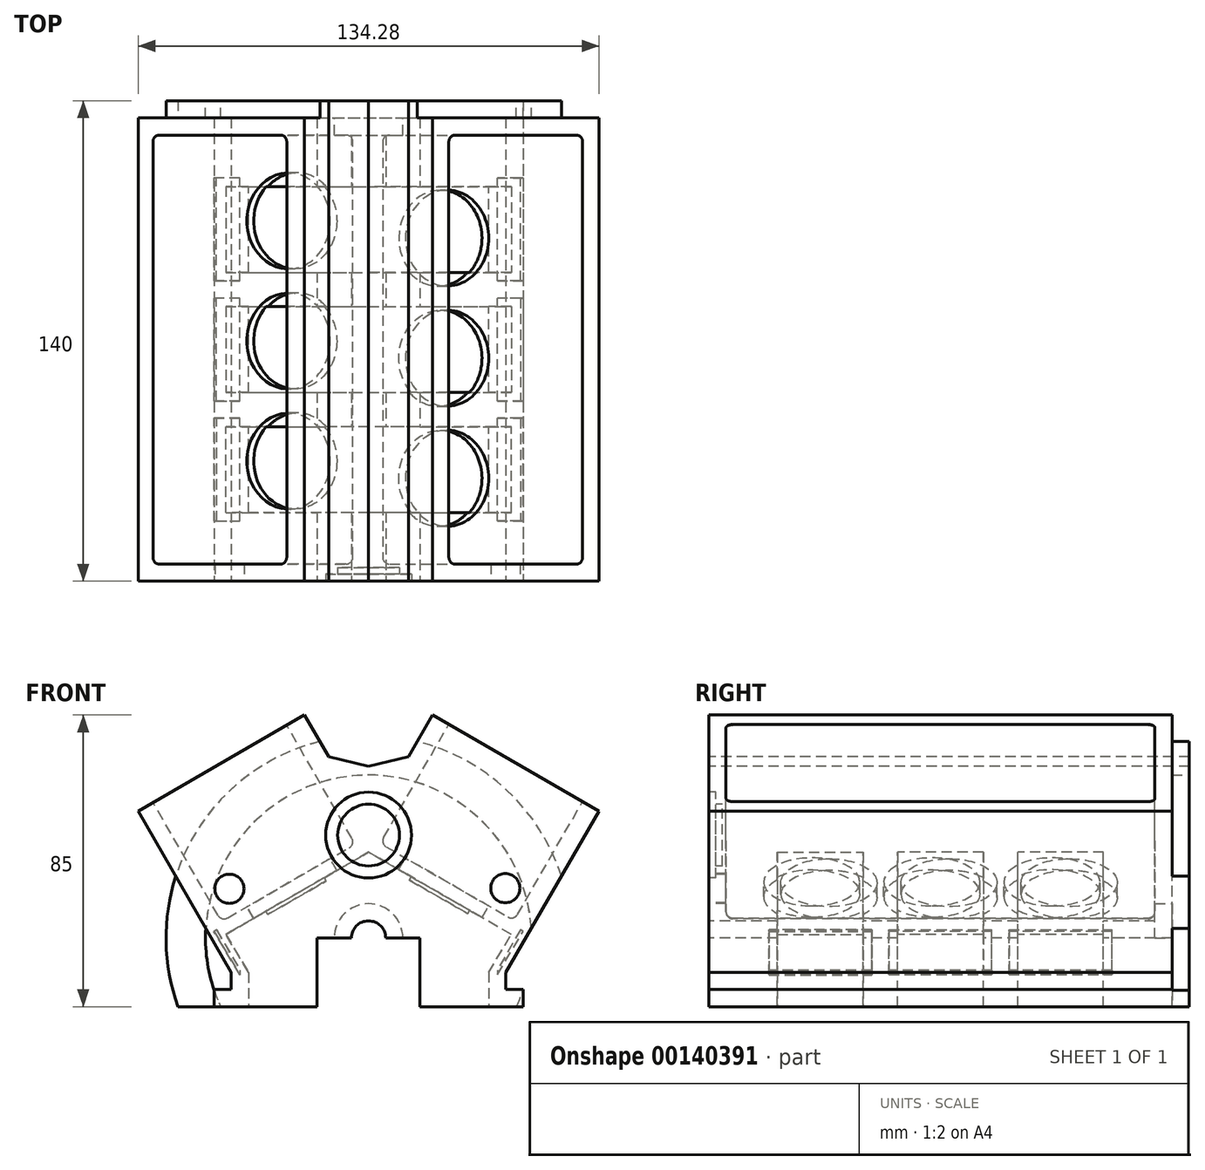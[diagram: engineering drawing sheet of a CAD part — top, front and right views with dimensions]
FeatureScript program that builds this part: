
annotation { "Feature Type Name" : "Feature", "Feature Type Description" : "" }
export const myFeature = defineFeature(function(context is Context, id is Id, definition is map)
    precondition{}
    {
        {
            var Q0;
            Q0=qCreatedBy(makeId("Front.planeOp"),FACE);
            var sketch = newSketch(context, id + "F0", { "sketchPlane" : qUnion([Q0])});
            skLineSegment(sketch, "E0", {"start": v(0, 0) * mm, "end": v(0, -20) * mm, "construction": true});
            skLineSegment(sketch, "E1", {"start": v(0, 0) * mm, "end": v(0, 50) * mm, "construction": true});
            skLineSegment(sketch, "E2", {"start": v(11.64, 52.88) * mm, "end": v(18.64, 65) * mm});
            skLineSegment(sketch, "E3", {"start": v(18.64, 65) * mm, "end": v(67.14, 37) * mm});
            skLineSegment(sketch, "E4", {"start": v(0, -20) * mm, "end": v(45, -20) * mm});
            skLineSegment(sketch, "E5", {"start": v(45, -20) * mm, "end": v(45, -15) * mm});
            skLineSegment(sketch, "E6", {"start": v(45, -15) * mm, "end": v(40, -15) * mm});
            skLineSegment(sketch, "E7", {"start": v(40, -15) * mm, "end": v(40, -10) * mm});
            skLineSegment(sketch, "E8", {"start": v(40, -10) * mm, "end": v(67.14, 37) * mm});
            skLineSegment(sketch, "E9", {"start": v(0, 50) * mm, "end": v(11.64, 52.88) * mm});
            skLineSegment(sketch, "E10.MirrorCS", {"start": v(0, 50) * mm, "end": v(-11.64, 52.88) * mm});
            skLineSegment(sketch, "E11.MirrorCS", {"start": v(-11.64, 52.88) * mm, "end": v(-18.64, 65) * mm});
            skLineSegment(sketch, "E12.MirrorCS", {"start": v(-18.64, 65) * mm, "end": v(-67.14, 37) * mm});
            skLineSegment(sketch, "E13.MirrorCS", {"start": v(-40, -10) * mm, "end": v(-67.14, 37) * mm});
            skLineSegment(sketch, "E14.MirrorCS", {"start": v(-40, -15) * mm, "end": v(-40, -10) * mm});
            skLineSegment(sketch, "E15.MirrorCS", {"start": v(-45, -15) * mm, "end": v(-40, -15) * mm});
            skLineSegment(sketch, "E16.MirrorCS", {"start": v(-45, -20) * mm, "end": v(-45, -15) * mm});
            skLineSegment(sketch, "E17.MirrorCS", {"start": v(0, -20) * mm, "end": v(-45, -20) * mm});
            skSolve(sketch);
        }
        {
            var Q0;
            Q0=makeQuery(id+"F0.imprint","IMPRINT",FACE,{"disambiguationData":[TD([[makeQuery(id+"F0.imprint","IMPRINT",EDGE,{"derivedFrom":sQuery(id+"F0.wireOp",EDGE,"E2")}),-1.0]])]});
            extrude(context, id + "F1", {"entities" : qUnion([Q0]), "oppositeDirection" : true, "depth" : 135 * mm});
        }
        {
            var Q0;
            Q0=makeQuery(id+"F1.opExtrude","SWEPT_FACE",FACE,{"disambiguationData":[OSD([sQuery(id+"F0.wireOp",EDGE,"E4"),sQuery(id+"F0.wireOp",EDGE,"E17.MirrorCS")])]});
            var sketch = newSketch(context, id + "F2", { "sketchPlane" : qUnion([Q0])});
            skLineSegment(sketch, "E18.bottom", {"start": v(-35, -20) * mm, "end": v(35, -20) * mm});
            skLineSegment(sketch, "E18.top", {"start": v(-35, -45) * mm, "end": v(35, -45) * mm});
            skLineSegment(sketch, "E18.left", {"start": v(-35, -20) * mm, "end": v(-35, -45) * mm});
            skLineSegment(sketch, "E18.right", {"start": v(35, -20) * mm, "end": v(35, -45) * mm});
            skPoint(sketch, "E18.middle", {"position": v(0, -32.5) * mm});
            skLineSegment(sketch, "E19.bottom", {"start": v(-35, -55) * mm, "end": v(35, -55) * mm});
            skLineSegment(sketch, "E19.top", {"start": v(-35, -80) * mm, "end": v(35, -80) * mm});
            skLineSegment(sketch, "E19.left", {"start": v(-35, -55) * mm, "end": v(-35, -80) * mm});
            skLineSegment(sketch, "E19.right", {"start": v(35, -55) * mm, "end": v(35, -80) * mm});
            skPoint(sketch, "E19.middle", {"position": v(0, -67.5) * mm});
            skLineSegment(sketch, "E20.bottom", {"start": v(-35, -90) * mm, "end": v(35, -90) * mm});
            skLineSegment(sketch, "E20.top", {"start": v(-35, -115) * mm, "end": v(35, -115) * mm});
            skLineSegment(sketch, "E20.left", {"start": v(-35, -90) * mm, "end": v(-35, -115) * mm});
            skLineSegment(sketch, "E20.right", {"start": v(35, -90) * mm, "end": v(35, -115) * mm});
            skPoint(sketch, "E20.middle", {"position": v(0, -102.5) * mm});
            skPoint(sketch, "E20.middle.positionSnap0", {"position": v(0, -80) * mm});
            skPoint(sketch, "E20.centerSnap0", {"position": v(0, -80) * mm});
            skSolve(sketch);
        }
        {
            var Q0;
            Q0 = qSketchRegion(id + "F2", true);
            extrude(context, id + "F3", {"entities" : qUnion([Q0]), "operationType" : NewBodyOperationType.REMOVE, "oppositeDirection" : true, "depth" : 10 * mm});
        }
        {
            var Q0;
            Q0=makeQuery(id+"F1.opExtrude","SWEPT_FACE",FACE,{"disambiguationData":[OSD([sQuery(id+"F0.wireOp",EDGE,"E3")])]});
            var sketch = newSketch(context, id + "F4", { "sketchPlane" : qUnion([Q0])});
            skLineSegment(sketch, "E21.bottom", {"start": v(-10.86, 130) * mm, "end": v(34.14, 130) * mm});
            skLineSegment(sketch, "E21.top", {"start": v(-10.86, 5) * mm, "end": v(34.14, 5) * mm});
            skLineSegment(sketch, "E21.left", {"start": v(-10.86, 130) * mm, "end": v(-10.86, 5) * mm});
            skLineSegment(sketch, "E21.right", {"start": v(34.14, 130) * mm, "end": v(34.14, 5) * mm});
            skPoint(sketch, "E21.middle.positionSnap0", {"position": v(11.64, 0) * mm});
            skPoint(sketch, "E21.centerSnap0", {"position": v(11.64, 0) * mm});
            skSolve(sketch);
        }
        {
            var Q0;
            Q0=makeQuery(id+"F4.imprint","IMPRINT",FACE,{"disambiguationData":[TD([[makeQuery(id+"F4.imprint","IMPRINT",EDGE,{"derivedFrom":sQuery(id+"F4.wireOp",EDGE,"E21.bottom")}),-1.0]])]});
            extrude(context, id + "F5", {"entities" : qUnion([Q0]), "operationType" : NewBodyOperationType.REMOVE, "oppositeDirection" : true, "depth" : 40 * mm});
        }
        {
            var Q0;
            Q0=makeQuery(id+"F1.opExtrude","SWEPT_FACE",FACE,{"disambiguationData":[OSD([sQuery(id+"F0.wireOp",EDGE,"E12.MirrorCS")])]});
            var sketch = newSketch(context, id + "F6", { "sketchPlane" : qUnion([Q0])});
            skLineSegment(sketch, "E22.bottom", {"start": v(-34.64, 130) * mm, "end": v(10.36, 130) * mm});
            skLineSegment(sketch, "E22.top", {"start": v(-34.64, 5) * mm, "end": v(10.36, 5) * mm});
            skLineSegment(sketch, "E22.left", {"start": v(-34.64, 130) * mm, "end": v(-34.64, 5) * mm});
            skLineSegment(sketch, "E22.right", {"start": v(10.36, 130) * mm, "end": v(10.36, 5) * mm});
            skPoint(sketch, "E22.middle", {"position": v(-12.14, 67.5) * mm});
            skPoint(sketch, "E22.middle.positionSnap0", {"position": v(-39.64, 67.5) * mm});
            skPoint(sketch, "E22.centerSnap0", {"position": v(-39.64, 67.5) * mm});
            skSolve(sketch);
        }
        {
            var Q0;
            Q0=makeQuery(id+"F6.imprint","IMPRINT",FACE,{"disambiguationData":[TD([[makeQuery(id+"F6.imprint","IMPRINT",EDGE,{"derivedFrom":sQuery(id+"F6.wireOp",EDGE,"E22.bottom")}),-1.0]])]});
            extrude(context, id + "F7", {"entities" : qUnion([Q0]), "operationType" : NewBodyOperationType.REMOVE, "oppositeDirection" : true, "depth" : 40 * mm});
        }
        {
            var Q0;
            Q0=makeQuery(id+"F1.opExtrude","CAP_FACE",FACE,{"disambiguationData":[OSD([sQuery(id+"F0.wireOp",EDGE,"E2"),sQuery(id+"F0.wireOp",EDGE,"E3"),sQuery(id+"F0.wireOp",EDGE,"E4"),sQuery(id+"F0.wireOp",EDGE,"E5"),sQuery(id+"F0.wireOp",EDGE,"E6"),sQuery(id+"F0.wireOp",EDGE,"E7"),sQuery(id+"F0.wireOp",EDGE,"E8"),sQuery(id+"F0.wireOp",EDGE,"E9"),sQuery(id+"F0.wireOp",EDGE,"E10.MirrorCS"),sQuery(id+"F0.wireOp",EDGE,"E11.MirrorCS"),sQuery(id+"F0.wireOp",EDGE,"E12.MirrorCS"),sQuery(id+"F0.wireOp",EDGE,"E13.MirrorCS"),sQuery(id+"F0.wireOp",EDGE,"E14.MirrorCS"),sQuery(id+"F0.wireOp",EDGE,"E15.MirrorCS"),sQuery(id+"F0.wireOp",EDGE,"E16.MirrorCS"),sQuery(id+"F0.wireOp",EDGE,"E17.MirrorCS")])],"isStart":true});
            var sketch = newSketch(context, id + "F8", { "sketchPlane" : qUnion([Q0])});
            skCircle(sketch, "E23", {"center": v(0, 0) * mm, "radius": 5 * mm});
            skSolve(sketch);
        }
        {
            var Q0;
            Q0=makeQuery(id+"F8.imprint","IMPRINT",FACE,{"disambiguationData":[TD([[makeQuery(id+"F8.imprint","IMPRINT",EDGE,{"derivedFrom":sQuery(id+"F8.wireOp",EDGE,"E23")}),1.0]])]});
            extrude(context, id + "F9", {"entities" : qUnion([Q0]), "operationType" : NewBodyOperationType.REMOVE, "oppositeDirection" : true, "depth" : 135 * mm});
        }
        {
            var Q0;
            Q0=makeQuery(id+"F1.opExtrude","CAP_FACE",FACE,{"disambiguationData":[OSD([sQuery(id+"F0.wireOp",EDGE,"E2"),sQuery(id+"F0.wireOp",EDGE,"E3"),sQuery(id+"F0.wireOp",EDGE,"E4"),sQuery(id+"F0.wireOp",EDGE,"E5"),sQuery(id+"F0.wireOp",EDGE,"E6"),sQuery(id+"F0.wireOp",EDGE,"E7"),sQuery(id+"F0.wireOp",EDGE,"E8"),sQuery(id+"F0.wireOp",EDGE,"E9"),sQuery(id+"F0.wireOp",EDGE,"E10.MirrorCS"),sQuery(id+"F0.wireOp",EDGE,"E11.MirrorCS"),sQuery(id+"F0.wireOp",EDGE,"E12.MirrorCS"),sQuery(id+"F0.wireOp",EDGE,"E13.MirrorCS"),sQuery(id+"F0.wireOp",EDGE,"E14.MirrorCS"),sQuery(id+"F0.wireOp",EDGE,"E15.MirrorCS"),sQuery(id+"F0.wireOp",EDGE,"E16.MirrorCS"),sQuery(id+"F0.wireOp",EDGE,"E17.MirrorCS")])],"isStart":true});
            var sketch = newSketch(context, id + "F10", { "sketchPlane" : qUnion([Q0])});
            skLineSegment(sketch, "E24.bottom", {"start": v(-15, 0) * mm, "end": v(15, 0) * mm});
            skLineSegment(sketch, "E24.top", {"start": v(-15, -20) * mm, "end": v(15, -20) * mm});
            skLineSegment(sketch, "E24.left", {"start": v(-15, 0) * mm, "end": v(-15, -20) * mm});
            skLineSegment(sketch, "E24.right", {"start": v(15, 0) * mm, "end": v(15, -20) * mm});
            skSolve(sketch);
        }
        {
            var Q0;
            Q0=makeQuery(id+"F10.imprint","IMPRINT",FACE,{"disambiguationData":[TD([[makeQuery(id+"F10.imprint","IMPRINT",EDGE,{"derivedFrom":sQuery(id+"F10.wireOp",EDGE,"E24.top")}),-1.0]])]});
            extrude(context, id + "F11", {"entities" : qUnion([Q0]), "operationType" : NewBodyOperationType.REMOVE, "oppositeDirection" : true, "depth" : 135 * mm});
        }
        {
            var Q0;
            Q0=makeQuery(id+"F5.boolean.opBoolean","COPY",FACE,{"derivedFrom":makeQuery(id+"F5.opExtrude","CAP_FACE",FACE,{"disambiguationData":[OSD([sQuery(id+"F4.wireOp",EDGE,"E21.bottom"),sQuery(id+"F4.wireOp",EDGE,"E21.top"),sQuery(id+"F4.wireOp",EDGE,"E21.left"),sQuery(id+"F4.wireOp",EDGE,"E21.right")])],"isStart":false})});
            var sketch = newSketch(context, id + "F12", { "sketchPlane" : qUnion([Q0])});
            skCircle(sketch, "E25", {"center": v(11.64, 30) * mm, "radius": 14 * mm});
            skCircle(sketch, "E26", {"center": v(11.64, 65) * mm, "radius": 14 * mm});
            skCircle(sketch, "E27", {"center": v(11.64, 100) * mm, "radius": 14 * mm});
            skSolve(sketch);
        }
        {
            var Q0;
            Q0=makeQuery(id+"F12.imprint","IMPRINT",FACE,{"disambiguationData":[TD([[makeQuery(id+"F12.imprint","IMPRINT",EDGE,{"derivedFrom":sQuery(id+"F12.wireOp",EDGE,"E25")}),1.0]])]});
            var Q1;
            Q1=makeQuery(id+"F12.imprint","IMPRINT",FACE,{"disambiguationData":[TD([[makeQuery(id+"F12.imprint","IMPRINT",EDGE,{"derivedFrom":sQuery(id+"F12.wireOp",EDGE,"E26")}),1.0]])]});
            var Q2;
            Q2=makeQuery(id+"F12.imprint","IMPRINT",FACE,{"disambiguationData":[TD([[makeQuery(id+"F12.imprint","IMPRINT",EDGE,{"derivedFrom":sQuery(id+"F12.wireOp",EDGE,"E27")}),1.0]])]});
            extrude(context, id + "F13", {"entities" : qUnion([Q0, Q1, Q2]), "operationType" : NewBodyOperationType.REMOVE, "oppositeDirection" : true, "depth" : 5 * mm});
        }
        {
            var Q0;
            Q0=makeQuery(id+"F7.boolean.opBoolean","COPY",FACE,{"derivedFrom":makeQuery(id+"F7.opExtrude","CAP_FACE",FACE,{"disambiguationData":[OSD([sQuery(id+"F6.wireOp",EDGE,"E22.bottom"),sQuery(id+"F6.wireOp",EDGE,"E22.top"),sQuery(id+"F6.wireOp",EDGE,"E22.left"),sQuery(id+"F6.wireOp",EDGE,"E22.right")])],"isStart":false})});
            var sketch = newSketch(context, id + "F14", { "sketchPlane" : qUnion([Q0])});
            skCircle(sketch, "E28", {"center": v(-12.14, 105) * mm, "radius": 14 * mm});
            skCircle(sketch, "E29", {"center": v(-12.14, 70) * mm, "radius": 14 * mm});
            skCircle(sketch, "E30", {"center": v(-12.14, 35) * mm, "radius": 14 * mm});
            skSolve(sketch);
        }
        {
            var Q0;
            Q0=makeQuery(id+"F14.imprint","IMPRINT",FACE,{"disambiguationData":[TD([[makeQuery(id+"F14.imprint","IMPRINT",EDGE,{"derivedFrom":sQuery(id+"F14.wireOp",EDGE,"E28")}),1.0]])]});
            var Q1;
            Q1=makeQuery(id+"F14.imprint","IMPRINT",FACE,{"disambiguationData":[TD([[makeQuery(id+"F14.imprint","IMPRINT",EDGE,{"derivedFrom":sQuery(id+"F14.wireOp",EDGE,"E29")}),1.0]])]});
            var Q2;
            Q2=makeQuery(id+"F14.imprint","IMPRINT",FACE,{"disambiguationData":[TD([[makeQuery(id+"F14.imprint","IMPRINT",EDGE,{"derivedFrom":sQuery(id+"F14.wireOp",EDGE,"E30")}),1.0]])]});
            extrude(context, id + "F15", {"entities" : qUnion([Q0, Q1, Q2]), "operationType" : NewBodyOperationType.REMOVE, "oppositeDirection" : true, "depth" : 5 * mm});
        }
        {
            var Q0;
            {var subQ0=sQuery(id+"F2.wireOp",EDGE,"E18.right");var subQ1=sQuery(id+"F2.wireOp",EDGE,"E18.top");Q0=makeQuery(id+"F11.boolean.opBoolean","SPLIT",FACE,{"disambiguationData":[TD([makeQuery(id+"F3.boolean.opBoolean","COPY",FACE,{"derivedFrom":makeQuery(id+"F3.opExtrude","SWEPT_FACE",FACE,{"disambiguationData":[OSD([subQ0])]})})])],"derivedFrom":makeQuery(id+"F3.boolean.opBoolean","COPY",FACE,{"derivedFrom":makeQuery(id+"F3.opExtrude","SWEPT_FACE",FACE,{"disambiguationData":[OSD([subQ1])]})})});}
            var sketch = newSketch(context, id + "F16", { "sketchPlane" : qUnion([Q0])});
            skLineSegment(sketch, "E31", {"start": v(35, -10) * mm, "end": v(41.62, 1.07) * mm});
            skLineSegment(sketch, "E32", {"start": v(41.62, 1.07) * mm, "end": v(0, 24.98) * mm});
            skLineSegment(sketch, "E33", {"start": v(0, 24.98) * mm, "end": v(-41.6, 1.04) * mm});
            skLineSegment(sketch, "E34", {"start": v(-41.6, 1.04) * mm, "end": v(-35, -10.05) * mm});
            skLineSegment(sketch, "E35", {"start": v(-35, -10.05) * mm, "end": v(35, -10) * mm});
            skLineSegment(sketch, "E36", {"start": v(0, 24.98) * mm, "end": v(0.02, -10.02) * mm, "construction": true});
            skSolve(sketch);
        }
        {
            var Q0;
            Q0=makeQuery(id+"F16.imprint","IMPRINT",FACE,{"disambiguationData":[TD([[makeQuery(id+"F16.imprint","IMPRINT",EDGE,{"derivedFrom":sQuery(id+"F16.wireOp",EDGE,"E31")}),1.0]])]});
            extrude(context, id + "F17", {"entities" : qUnion([Q0]), "operationType" : NewBodyOperationType.REMOVE, "depth" : 25 * mm});
        }
        {
            var Q0;
            {var subQ0=sQuery(id+"F2.wireOp",EDGE,"E19.right");var subQ1=sQuery(id+"F2.wireOp",EDGE,"E19.bottom");Q0=makeQuery(id+"F11.boolean.opBoolean","SPLIT",FACE,{"disambiguationData":[TD([makeQuery(id+"F3.boolean.opBoolean","COPY",FACE,{"derivedFrom":makeQuery(id+"F3.opExtrude","SWEPT_FACE",FACE,{"disambiguationData":[OSD([subQ0])]})})])],"derivedFrom":makeQuery(id+"F3.boolean.opBoolean","COPY",FACE,{"derivedFrom":makeQuery(id+"F3.opExtrude","SWEPT_FACE",FACE,{"disambiguationData":[OSD([subQ1])]})})});}
            var sketch = newSketch(context, id + "F18", { "sketchPlane" : qUnion([Q0])});
            skLineSegment(sketch, "E37", {"start": v(-35, -10) * mm, "end": v(35, -10) * mm});
            skLineSegment(sketch, "E38", {"start": v(35, -10) * mm, "end": v(41.61, 1.08) * mm});
            skLineSegment(sketch, "E39", {"start": v(41.61, 1.08) * mm, "end": v(0, 25) * mm});
            skLineSegment(sketch, "E40", {"start": v(0, 25) * mm, "end": v(-41.61, 1.08) * mm});
            skLineSegment(sketch, "E41", {"start": v(-41.61, 1.08) * mm, "end": v(-35, -10) * mm});
            skLineSegment(sketch, "E42", {"start": v(0, 25) * mm, "end": v(0, -10) * mm, "construction": true});
            skSolve(sketch);
        }
        {
            var Q0;
            Q0 = qSketchRegion(id + "F18", true);
            extrude(context, id + "F19", {"entities" : qUnion([Q0]), "operationType" : NewBodyOperationType.REMOVE, "depth" : 25 * mm});
        }
        {
            var Q0;
            {var subQ0=sQuery(id+"F2.wireOp",EDGE,"E20.right");var subQ1=sQuery(id+"F2.wireOp",EDGE,"E20.bottom");Q0=makeQuery(id+"F11.boolean.opBoolean","SPLIT",FACE,{"disambiguationData":[TD([makeQuery(id+"F3.boolean.opBoolean","COPY",FACE,{"derivedFrom":makeQuery(id+"F3.opExtrude","SWEPT_FACE",FACE,{"disambiguationData":[OSD([subQ0])]})})])],"derivedFrom":makeQuery(id+"F3.boolean.opBoolean","COPY",FACE,{"derivedFrom":makeQuery(id+"F3.opExtrude","SWEPT_FACE",FACE,{"disambiguationData":[OSD([subQ1])]})})});}
            var sketch = newSketch(context, id + "F20", { "sketchPlane" : qUnion([Q0])});
            skLineSegment(sketch, "E43", {"start": v(-35, -10) * mm, "end": v(35, -10) * mm});
            skLineSegment(sketch, "E44", {"start": v(0, 25) * mm, "end": v(0, -10) * mm, "construction": true});
            skLineSegment(sketch, "E45", {"start": v(-35, -10) * mm, "end": v(-41.61, 1.08) * mm});
            skLineSegment(sketch, "E46", {"start": v(-41.61, 1.08) * mm, "end": v(0, 25) * mm});
            skLineSegment(sketch, "E47", {"start": v(35, -10) * mm, "end": v(41.61, 1.08) * mm});
            skLineSegment(sketch, "E48", {"start": v(41.61, 1.08) * mm, "end": v(0, 25) * mm});
            skSolve(sketch);
        }
        {
            var Q0;
            {var subQ0=sQuery(id+"F20.wireOp",EDGE,"E45");Q0=makeQuery(id+"F20.imprint","IMPRINT",FACE,{"disambiguationData":[TD([[makeQuery(id+"F20.imprint","IMPRINT",EDGE,{"derivedFrom":subQ0}),-1.0]])]});}
            extrude(context, id + "F21", {"entities" : qUnion([Q0]), "operationType" : NewBodyOperationType.REMOVE, "depth" : 25 * mm});
        }
        {
            var Q0;
            Q0=makeQuery(id+"F5.boolean.opBoolean","COPY",EDGE,{"derivedFrom":makeQuery(id+"F5.opExtrude","SWEPT_EDGE",EDGE,{"disambiguationData":[OSD([sQuery(id+"F4.wireOp",EDGE,"E21.bottom"),sQuery(id+"F4.wireOp",EDGE,"E21.left")])]})});
            var Q1;
            Q1=makeQuery(id+"F5.boolean.opBoolean","COPY",EDGE,{"derivedFrom":makeQuery(id+"F5.opExtrude","CAP_EDGE",EDGE,{"disambiguationData":[OSD([sQuery(id+"F4.wireOp",EDGE,"E21.bottom")])],"isStart":false})});
            var Q2;
            Q2=makeQuery(id+"F5.boolean.opBoolean","COPY",EDGE,{"derivedFrom":makeQuery(id+"F5.opExtrude","CAP_EDGE",EDGE,{"disambiguationData":[OSD([sQuery(id+"F4.wireOp",EDGE,"E21.left")])],"isStart":false})});
            var Q3;
            Q3=makeQuery(id+"F5.boolean.opBoolean","COPY",EDGE,{"derivedFrom":makeQuery(id+"F5.opExtrude","CAP_EDGE",EDGE,{"disambiguationData":[OSD([sQuery(id+"F4.wireOp",EDGE,"E21.top")])],"isStart":false})});
            var Q4;
            Q4=makeQuery(id+"F5.boolean.opBoolean","COPY",EDGE,{"derivedFrom":makeQuery(id+"F5.opExtrude","SWEPT_EDGE",EDGE,{"disambiguationData":[OSD([sQuery(id+"F4.wireOp",EDGE,"E21.top"),sQuery(id+"F4.wireOp",EDGE,"E21.left")])]})});
            var Q5;
            Q5=makeQuery(id+"F5.boolean.opBoolean","COPY",EDGE,{"derivedFrom":makeQuery(id+"F5.opExtrude","SWEPT_EDGE",EDGE,{"disambiguationData":[OSD([sQuery(id+"F4.wireOp",EDGE,"E21.bottom"),sQuery(id+"F4.wireOp",EDGE,"E21.right")])]})});
            var Q6;
            Q6=makeQuery(id+"F5.boolean.opBoolean","COPY",EDGE,{"derivedFrom":makeQuery(id+"F5.opExtrude","CAP_EDGE",EDGE,{"disambiguationData":[OSD([sQuery(id+"F4.wireOp",EDGE,"E21.right")])],"isStart":false})});
            var Q7;
            Q7=makeQuery(id+"F5.boolean.opBoolean","COPY",EDGE,{"derivedFrom":makeQuery(id+"F5.opExtrude","SWEPT_EDGE",EDGE,{"disambiguationData":[OSD([sQuery(id+"F4.wireOp",EDGE,"E21.top"),sQuery(id+"F4.wireOp",EDGE,"E21.right")])]})});
            fillet(context, id + "F22", {"entities" : qUnion([Q0, Q1, Q2, Q3, Q4, Q5, Q6, Q7]), "radius" : 2 * mm, "tangentPropagation" : true, "allowEdgeOverflow" : false});
        }
        {
            var Q0;
            Q0=makeQuery(id+"F7.boolean.opBoolean","COPY",EDGE,{"derivedFrom":makeQuery(id+"F7.opExtrude","SWEPT_EDGE",EDGE,{"disambiguationData":[OSD([sQuery(id+"F6.wireOp",EDGE,"E22.bottom"),sQuery(id+"F6.wireOp",EDGE,"E22.left")])]})});
            var Q1;
            Q1=makeQuery(id+"F7.boolean.opBoolean","COPY",EDGE,{"derivedFrom":makeQuery(id+"F7.opExtrude","CAP_EDGE",EDGE,{"disambiguationData":[OSD([sQuery(id+"F6.wireOp",EDGE,"E22.bottom")])],"isStart":false})});
            var Q2;
            Q2=makeQuery(id+"F7.boolean.opBoolean","COPY",EDGE,{"derivedFrom":makeQuery(id+"F7.opExtrude","CAP_EDGE",EDGE,{"disambiguationData":[OSD([sQuery(id+"F6.wireOp",EDGE,"E22.left")])],"isStart":false})});
            var Q3;
            Q3=makeQuery(id+"F7.boolean.opBoolean","COPY",EDGE,{"derivedFrom":makeQuery(id+"F7.opExtrude","SWEPT_EDGE",EDGE,{"disambiguationData":[OSD([sQuery(id+"F6.wireOp",EDGE,"E22.bottom"),sQuery(id+"F6.wireOp",EDGE,"E22.right")])]})});
            var Q4;
            Q4=makeQuery(id+"F7.boolean.opBoolean","COPY",EDGE,{"derivedFrom":makeQuery(id+"F7.opExtrude","CAP_EDGE",EDGE,{"disambiguationData":[OSD([sQuery(id+"F6.wireOp",EDGE,"E22.right")])],"isStart":false})});
            var Q5;
            Q5=makeQuery(id+"F7.boolean.opBoolean","COPY",EDGE,{"derivedFrom":makeQuery(id+"F7.opExtrude","CAP_EDGE",EDGE,{"disambiguationData":[OSD([sQuery(id+"F6.wireOp",EDGE,"E22.top")])],"isStart":false})});
            var Q6;
            Q6=makeQuery(id+"F7.boolean.opBoolean","COPY",EDGE,{"derivedFrom":makeQuery(id+"F7.opExtrude","SWEPT_EDGE",EDGE,{"disambiguationData":[OSD([sQuery(id+"F6.wireOp",EDGE,"E22.top"),sQuery(id+"F6.wireOp",EDGE,"E22.left")])]})});
            var Q7;
            Q7=makeQuery(id+"F7.boolean.opBoolean","COPY",EDGE,{"derivedFrom":makeQuery(id+"F7.opExtrude","SWEPT_EDGE",EDGE,{"disambiguationData":[OSD([sQuery(id+"F6.wireOp",EDGE,"E22.top"),sQuery(id+"F6.wireOp",EDGE,"E22.right")])]})});
            fillet(context, id + "F23", {"entities" : qUnion([Q0, Q1, Q2, Q3, Q4, Q5, Q6, Q7]), "radius" : 2 * mm, "tangentPropagation" : true, "allowEdgeOverflow" : false});
        }
        {
            var Q0;
            Q0=makeQuery(id+"F5.boolean.opBoolean","COPY",FACE,{"derivedFrom":makeQuery(id+"F5.opExtrude","SWEPT_FACE",FACE,{"disambiguationData":[OSD([sQuery(id+"F4.wireOp",EDGE,"E21.top")])]})});
            var Q1;
            {var subQ2=sQuery(id+"F10.wireOp",EDGE,"E24.left");Q1=makeQuery(id+"F17.boolean.opBoolean","SPLIT",FACE,{"disambiguationData":[TD([makeQuery(id+"F3.boolean.opBoolean","COPY",FACE,{"derivedFrom":makeQuery(id+"F3.opExtrude","SWEPT_FACE",FACE,{"disambiguationData":[OSD([sQuery(id+"F2.wireOp",EDGE,"E18.bottom")])]})})])],"derivedFrom":makeQuery(id+"F11.boolean.opBoolean","COPY",FACE,{"derivedFrom":makeQuery(id+"F11.opExtrude","SWEPT_FACE",FACE,{"disambiguationData":[OSD([subQ2])]})})});}
            var Q2;
            Q2=makeQuery(id+"F1.opExtrude","SWEPT_FACE",FACE,{"disambiguationData":[OSD([sQuery(id+"F0.wireOp",EDGE,"E12.MirrorCS")])]});
            var Q3;
            Q3=makeQuery(id+"F5.boolean.opBoolean","COPY",FACE,{"derivedFrom":makeQuery(id+"F5.opExtrude","SWEPT_FACE",FACE,{"disambiguationData":[OSD([sQuery(id+"F4.wireOp",EDGE,"E21.bottom")])]})});
            var Q4;
            {var subQ0=sQuery(id+"F6.wireOp",EDGE,"E22.left");var subQ1=sQuery(id+"F6.wireOp",EDGE,"E22.bottom");Q4=makeQuery(id+"F23.opFillet","BLEND_FACE",FACE,{"disambiguationData":[OSD([subQ1,subQ0]),TDD([makeQuery(id+"F7.boolean.opBoolean","COPY",EDGE,{"derivedFrom":makeQuery(id+"F7.opExtrude","SWEPT_EDGE",EDGE,{"disambiguationData":[OSD([subQ1,subQ0])]})})])]});}
            var Q5;
            {var subQ1=sQuery(id+"F2.wireOp",EDGE,"E20.right");var subQ2=sQuery(id+"F2.wireOp",EDGE,"E20.left");var subQ3=sQuery(id+"F2.wireOp",EDGE,"E20.top");var subQ5=makeQuery(id+"F3.boolean.opBoolean","COPY",FACE,{"derivedFrom":makeQuery(id+"F3.opExtrude","SWEPT_FACE",FACE,{"disambiguationData":[OSD([subQ3])]})});Q5=makeQuery(id+"F21.boolean.opBoolean","MERGE",FACE,{"derivedFrom":[makeQuery(id+"F11.boolean.opBoolean","SPLIT",FACE,{"disambiguationData":[TD([makeQuery(id+"F3.boolean.opBoolean","COPY",FACE,{"derivedFrom":makeQuery(id+"F3.opExtrude","SWEPT_FACE",FACE,{"disambiguationData":[OSD([subQ2])]})})])],"derivedFrom":subQ5}),makeQuery(id+"F11.boolean.opBoolean","SPLIT",FACE,{"disambiguationData":[TD([makeQuery(id+"F3.boolean.opBoolean","COPY",FACE,{"derivedFrom":makeQuery(id+"F3.opExtrude","SWEPT_FACE",FACE,{"disambiguationData":[OSD([subQ1])]})})])],"derivedFrom":subQ5}),makeQuery(id+"F21.opExtrude","CAP_FACE",FACE,{"disambiguationData":[OSD([sQuery(id+"F20.wireOp",EDGE,"E43"),sQuery(id+"F20.wireOp",EDGE,"E45"),sQuery(id+"F20.wireOp",EDGE,"E46"),sQuery(id+"F20.wireOp",EDGE,"E47"),sQuery(id+"F20.wireOp",EDGE,"E48")])],"isStart":false})]});}
            var Q6;
            {var subQ1=sQuery(id+"F2.wireOp",EDGE,"E19.right");var subQ2=sQuery(id+"F2.wireOp",EDGE,"E19.left");var subQ3=sQuery(id+"F2.wireOp",EDGE,"E19.top");var subQ5=makeQuery(id+"F3.boolean.opBoolean","COPY",FACE,{"derivedFrom":makeQuery(id+"F3.opExtrude","SWEPT_FACE",FACE,{"disambiguationData":[OSD([subQ3])]})});Q6=makeQuery(id+"F19.boolean.opBoolean","MERGE",FACE,{"derivedFrom":[makeQuery(id+"F11.boolean.opBoolean","SPLIT",FACE,{"disambiguationData":[TD([makeQuery(id+"F3.boolean.opBoolean","COPY",FACE,{"derivedFrom":makeQuery(id+"F3.opExtrude","SWEPT_FACE",FACE,{"disambiguationData":[OSD([subQ2])]})})])],"derivedFrom":subQ5}),makeQuery(id+"F11.boolean.opBoolean","SPLIT",FACE,{"disambiguationData":[TD([makeQuery(id+"F3.boolean.opBoolean","COPY",FACE,{"derivedFrom":makeQuery(id+"F3.opExtrude","SWEPT_FACE",FACE,{"disambiguationData":[OSD([subQ1])]})})])],"derivedFrom":subQ5}),makeQuery(id+"F19.opExtrude","CAP_FACE",FACE,{"disambiguationData":[OSD([sQuery(id+"F18.wireOp",EDGE,"E37"),sQuery(id+"F18.wireOp",EDGE,"E38"),sQuery(id+"F18.wireOp",EDGE,"E39"),sQuery(id+"F18.wireOp",EDGE,"E40"),sQuery(id+"F18.wireOp",EDGE,"E41")])],"isStart":false})]});}
            var Q7;
            Q7=makeQuery(id+"F1.opExtrude","SWEPT_FACE",FACE,{"disambiguationData":[OSD([sQuery(id+"F0.wireOp",EDGE,"E5")])]});
            var Q8;
            {var subQ0=sQuery(id+"F0.wireOp",EDGE,"E17.MirrorCS");var subQ1=sQuery(id+"F0.wireOp",EDGE,"E16.MirrorCS");var subQ13=sQuery(id+"F0.wireOp",EDGE,"E4");Q8=makeQuery(id+"F11.boolean.opBoolean","SPLIT",FACE,{"disambiguationData":[TD([makeQuery(id+"F1.opExtrude","SWEPT_FACE",FACE,{"disambiguationData":[OSD([subQ1])]})])],"derivedFrom":makeQuery(id+"F1.opExtrude","SWEPT_FACE",FACE,{"disambiguationData":[OSD([subQ13,subQ0])]})});}
            var Q9;
            Q9=makeQuery(id+"F1.opExtrude","SWEPT_FACE",FACE,{"disambiguationData":[OSD([sQuery(id+"F0.wireOp",EDGE,"E13.MirrorCS")])]});
            var Q10;
            Q10=makeQuery(id+"F19.boolean.opBoolean","COPY",FACE,{"derivedFrom":makeQuery(id+"F19.opExtrude","SWEPT_FACE",FACE,{"disambiguationData":[OSD([sQuery(id+"F18.wireOp",EDGE,"E40")])]})});
            var Q11;
            Q11=makeQuery(id+"F1.opExtrude","SWEPT_FACE",FACE,{"disambiguationData":[OSD([sQuery(id+"F0.wireOp",EDGE,"E9")])]});
            var Q12;
            Q12=makeQuery(id+"F1.opExtrude","SWEPT_FACE",FACE,{"disambiguationData":[OSD([sQuery(id+"F0.wireOp",EDGE,"E3")])]});
            var Q13;
            Q13=makeQuery(id+"F22.opFillet","BLEND_FACE",FACE,{"disambiguationData":[OSD([sQuery(id+"F4.wireOp",EDGE,"E21.bottom")])]});
            var Q14;
            {var subQ0=sQuery(id+"F0.wireOp",EDGE,"E17.MirrorCS");var subQ12=sQuery(id+"F0.wireOp",EDGE,"E5");var subQ13=sQuery(id+"F0.wireOp",EDGE,"E4");Q14=makeQuery(id+"F11.boolean.opBoolean","SPLIT",FACE,{"disambiguationData":[TD([makeQuery(id+"F1.opExtrude","SWEPT_FACE",FACE,{"disambiguationData":[OSD([subQ12])]})])],"derivedFrom":makeQuery(id+"F1.opExtrude","SWEPT_FACE",FACE,{"disambiguationData":[OSD([subQ13,subQ0])]})});}
            var Q15;
            Q15=makeQuery(id+"F1.opExtrude","SWEPT_FACE",FACE,{"disambiguationData":[OSD([sQuery(id+"F0.wireOp",EDGE,"E10.MirrorCS")])]});
            var Q16;
            Q16=makeQuery(id+"F1.opExtrude","CAP_FACE",FACE,{"disambiguationData":[OSD([sQuery(id+"F0.wireOp",EDGE,"E2"),sQuery(id+"F0.wireOp",EDGE,"E3"),sQuery(id+"F0.wireOp",EDGE,"E4"),sQuery(id+"F0.wireOp",EDGE,"E5"),sQuery(id+"F0.wireOp",EDGE,"E6"),sQuery(id+"F0.wireOp",EDGE,"E7"),sQuery(id+"F0.wireOp",EDGE,"E8"),sQuery(id+"F0.wireOp",EDGE,"E9"),sQuery(id+"F0.wireOp",EDGE,"E10.MirrorCS"),sQuery(id+"F0.wireOp",EDGE,"E11.MirrorCS"),sQuery(id+"F0.wireOp",EDGE,"E12.MirrorCS"),sQuery(id+"F0.wireOp",EDGE,"E13.MirrorCS"),sQuery(id+"F0.wireOp",EDGE,"E14.MirrorCS"),sQuery(id+"F0.wireOp",EDGE,"E15.MirrorCS"),sQuery(id+"F0.wireOp",EDGE,"E16.MirrorCS"),sQuery(id+"F0.wireOp",EDGE,"E17.MirrorCS")])],"isStart":true});
            var Q17;
            {var subQ2=sQuery(id+"F8.wireOp",EDGE,"E23");var subQ6=makeQuery(id+"F3.boolean.opBoolean","COPY",FACE,{"derivedFrom":makeQuery(id+"F3.opExtrude","SWEPT_FACE",FACE,{"disambiguationData":[OSD([sQuery(id+"F2.wireOp",EDGE,"E19.top")])]})});var subQ9=sQuery(id+"F2.wireOp",EDGE,"E18.top");Q17=makeQuery(id+"F21.boolean.opBoolean","SPLIT",FACE,{"disambiguationData":[TD([subQ6])],"derivedFrom":makeQuery(id+"F19.boolean.opBoolean","SPLIT",FACE,{"disambiguationData":[TD([subQ6])],"derivedFrom":makeQuery(id+"F17.boolean.opBoolean","SPLIT",FACE,{"disambiguationData":[TD([makeQuery(id+"F3.boolean.opBoolean","COPY",FACE,{"derivedFrom":makeQuery(id+"F3.opExtrude","SWEPT_FACE",FACE,{"disambiguationData":[OSD([subQ9])]})})])],"derivedFrom":makeQuery(id+"F9.boolean.opBoolean","COPY",FACE,{"derivedFrom":makeQuery(id+"F9.opExtrude","SWEPT_FACE",FACE,{"disambiguationData":[OSD([subQ2])]})})})})});}
            var Q18;
            Q18=makeQuery(id+"F22.opFillet","BLEND_FACE",FACE,{"disambiguationData":[OSD([sQuery(id+"F4.wireOp",EDGE,"E21.left")])]});
            var Q19;
            Q19=makeQuery(id+"F1.opExtrude","SWEPT_FACE",FACE,{"disambiguationData":[OSD([sQuery(id+"F0.wireOp",EDGE,"E6")])]});
            var Q20;
            {var subQ0=sQuery(id+"F10.wireOp",EDGE,"E24.right");var subQ6=sQuery(id+"F2.wireOp",EDGE,"E20.top");var subQ7=makeQuery(id+"F3.boolean.opBoolean","COPY",FACE,{"derivedFrom":makeQuery(id+"F3.opExtrude","SWEPT_FACE",FACE,{"disambiguationData":[OSD([subQ6])]})});var subQ9=sQuery(id+"F2.wireOp",EDGE,"E19.top");var subQ10=makeQuery(id+"F3.boolean.opBoolean","COPY",FACE,{"derivedFrom":makeQuery(id+"F3.opExtrude","SWEPT_FACE",FACE,{"disambiguationData":[OSD([subQ9])]})});var subQ15=sQuery(id+"F2.wireOp",EDGE,"E18.top");Q20=makeQuery(id+"F21.boolean.opBoolean","SPLIT",FACE,{"disambiguationData":[TD([subQ7])],"derivedFrom":makeQuery(id+"F19.boolean.opBoolean","SPLIT",FACE,{"disambiguationData":[TD([subQ10])],"derivedFrom":makeQuery(id+"F17.boolean.opBoolean","SPLIT",FACE,{"disambiguationData":[TD([makeQuery(id+"F3.boolean.opBoolean","COPY",FACE,{"derivedFrom":makeQuery(id+"F3.opExtrude","SWEPT_FACE",FACE,{"disambiguationData":[OSD([subQ15])]})})])],"derivedFrom":makeQuery(id+"F11.boolean.opBoolean","COPY",FACE,{"derivedFrom":makeQuery(id+"F11.opExtrude","SWEPT_FACE",FACE,{"disambiguationData":[OSD([subQ0])]})})})})});}
            var Q21;
            Q21=makeQuery(id+"F1.opExtrude","SWEPT_FACE",FACE,{"disambiguationData":[OSD([sQuery(id+"F0.wireOp",EDGE,"E11.MirrorCS")])]});
            var Q22;
            Q22=makeQuery(id+"F1.opExtrude","CAP_FACE",FACE,{"disambiguationData":[OSD([sQuery(id+"F0.wireOp",EDGE,"E2"),sQuery(id+"F0.wireOp",EDGE,"E3"),sQuery(id+"F0.wireOp",EDGE,"E4"),sQuery(id+"F0.wireOp",EDGE,"E5"),sQuery(id+"F0.wireOp",EDGE,"E6"),sQuery(id+"F0.wireOp",EDGE,"E7"),sQuery(id+"F0.wireOp",EDGE,"E8"),sQuery(id+"F0.wireOp",EDGE,"E9"),sQuery(id+"F0.wireOp",EDGE,"E10.MirrorCS"),sQuery(id+"F0.wireOp",EDGE,"E11.MirrorCS"),sQuery(id+"F0.wireOp",EDGE,"E12.MirrorCS"),sQuery(id+"F0.wireOp",EDGE,"E13.MirrorCS"),sQuery(id+"F0.wireOp",EDGE,"E14.MirrorCS"),sQuery(id+"F0.wireOp",EDGE,"E15.MirrorCS"),sQuery(id+"F0.wireOp",EDGE,"E16.MirrorCS"),sQuery(id+"F0.wireOp",EDGE,"E17.MirrorCS")])],"isStart":false});
            var Q23;
            Q23=makeQuery(id+"F13.boolean.opBoolean","COPY",FACE,{"derivedFrom":makeQuery(id+"F13.opExtrude","SWEPT_FACE",FACE,{"disambiguationData":[OSD([sQuery(id+"F12.wireOp",EDGE,"E26")])]})});
            var Q24;
            Q24=makeQuery(id+"F21.boolean.opBoolean","COPY",FACE,{"derivedFrom":makeQuery(id+"F21.opExtrude","SWEPT_FACE",FACE,{"disambiguationData":[OSD([sQuery(id+"F20.wireOp",EDGE,"E46")])]})});
            var Q25;
            Q25=makeQuery(id+"F13.boolean.opBoolean","COPY",FACE,{"derivedFrom":makeQuery(id+"F13.opExtrude","SWEPT_FACE",FACE,{"disambiguationData":[OSD([sQuery(id+"F12.wireOp",EDGE,"E27")])]})});
            var Q26;
            Q26=makeQuery(id+"F1.opExtrude","SWEPT_FACE",FACE,{"disambiguationData":[OSD([sQuery(id+"F0.wireOp",EDGE,"E8")])]});
            var Q27;
            Q27=makeQuery(id+"F5.boolean.opBoolean","COPY",FACE,{"derivedFrom":makeQuery(id+"F5.opExtrude","CAP_FACE",FACE,{"disambiguationData":[OSD([sQuery(id+"F4.wireOp",EDGE,"E21.bottom"),sQuery(id+"F4.wireOp",EDGE,"E21.top"),sQuery(id+"F4.wireOp",EDGE,"E21.left"),sQuery(id+"F4.wireOp",EDGE,"E21.right")])],"isStart":false})});
            var Q28;
            {var subQ2=sQuery(id+"F8.wireOp",EDGE,"E23");var subQ7=sQuery(id+"F2.wireOp",EDGE,"E18.top");Q28=makeQuery(id+"F21.boolean.opBoolean","SPLIT",FACE,{"disambiguationData":[TD([makeQuery(id+"F3.boolean.opBoolean","COPY",FACE,{"derivedFrom":makeQuery(id+"F3.opExtrude","SWEPT_FACE",FACE,{"disambiguationData":[OSD([sQuery(id+"F2.wireOp",EDGE,"E20.top")])]})})])],"derivedFrom":makeQuery(id+"F19.boolean.opBoolean","SPLIT",FACE,{"disambiguationData":[TD([makeQuery(id+"F3.boolean.opBoolean","COPY",FACE,{"derivedFrom":makeQuery(id+"F3.opExtrude","SWEPT_FACE",FACE,{"disambiguationData":[OSD([sQuery(id+"F2.wireOp",EDGE,"E19.top")])]})})])],"derivedFrom":makeQuery(id+"F17.boolean.opBoolean","SPLIT",FACE,{"disambiguationData":[TD([makeQuery(id+"F3.boolean.opBoolean","COPY",FACE,{"derivedFrom":makeQuery(id+"F3.opExtrude","SWEPT_FACE",FACE,{"disambiguationData":[OSD([subQ7])]})})])],"derivedFrom":makeQuery(id+"F9.boolean.opBoolean","COPY",FACE,{"derivedFrom":makeQuery(id+"F9.opExtrude","SWEPT_FACE",FACE,{"disambiguationData":[OSD([subQ2])]})})})})});}
            var Q29;
            Q29=makeQuery(id+"F7.boolean.opBoolean","COPY",FACE,{"derivedFrom":makeQuery(id+"F7.opExtrude","SWEPT_FACE",FACE,{"disambiguationData":[OSD([sQuery(id+"F6.wireOp",EDGE,"E22.top")])]})});
            var Q30;
            Q30=makeQuery(id+"F7.boolean.opBoolean","COPY",FACE,{"derivedFrom":makeQuery(id+"F7.opExtrude","SWEPT_FACE",FACE,{"disambiguationData":[OSD([sQuery(id+"F6.wireOp",EDGE,"E22.bottom")])]})});
            var Q31;
            Q31=makeQuery(id+"F5.boolean.opBoolean","COPY",FACE,{"derivedFrom":makeQuery(id+"F5.opExtrude","SWEPT_FACE",FACE,{"disambiguationData":[OSD([sQuery(id+"F4.wireOp",EDGE,"E21.left")])]})});
            var Q32;
            Q32=makeQuery(id+"F5.boolean.opBoolean","COPY",FACE,{"derivedFrom":makeQuery(id+"F5.opExtrude","SWEPT_FACE",FACE,{"disambiguationData":[OSD([sQuery(id+"F4.wireOp",EDGE,"E21.right")])]})});
            var Q33;
            Q33=makeQuery(id+"F1.opExtrude","SWEPT_FACE",FACE,{"disambiguationData":[OSD([sQuery(id+"F0.wireOp",EDGE,"E7")])]});
            var Q34;
            Q34=makeQuery(id+"F7.boolean.opBoolean","COPY",FACE,{"derivedFrom":makeQuery(id+"F7.opExtrude","SWEPT_FACE",FACE,{"disambiguationData":[OSD([sQuery(id+"F6.wireOp",EDGE,"E22.left")])]})});
            var Q35;
            Q35=makeQuery(id+"F7.boolean.opBoolean","COPY",FACE,{"derivedFrom":makeQuery(id+"F7.opExtrude","SWEPT_FACE",FACE,{"disambiguationData":[OSD([sQuery(id+"F6.wireOp",EDGE,"E22.right")])]})});
            var Q36;
            {var subQ0=sQuery(id+"F4.wireOp",EDGE,"E21.left");var subQ1=sQuery(id+"F4.wireOp",EDGE,"E21.bottom");Q36=makeQuery(id+"F22.opFillet","BLEND_FACE",FACE,{"disambiguationData":[OSD([subQ1,subQ0]),TDD([makeQuery(id+"F5.boolean.opBoolean","COPY",EDGE,{"derivedFrom":makeQuery(id+"F5.opExtrude","SWEPT_EDGE",EDGE,{"disambiguationData":[OSD([subQ1,subQ0])]})})])]});}
            var Q37;
            {var subQ0=sQuery(id+"F4.wireOp",EDGE,"E21.right");var subQ1=sQuery(id+"F4.wireOp",EDGE,"E21.bottom");Q37=makeQuery(id+"F22.opFillet","BLEND_FACE",FACE,{"disambiguationData":[OSD([subQ1,subQ0]),TDD([makeQuery(id+"F5.boolean.opBoolean","COPY",EDGE,{"derivedFrom":makeQuery(id+"F5.opExtrude","SWEPT_EDGE",EDGE,{"disambiguationData":[OSD([subQ1,subQ0])]})})])]});}
            var Q38;
            {var subQ0=sQuery(id+"F4.wireOp",EDGE,"E21.left");var subQ1=sQuery(id+"F4.wireOp",EDGE,"E21.top");Q38=makeQuery(id+"F22.opFillet","BLEND_FACE",FACE,{"disambiguationData":[OSD([subQ1,subQ0]),TDD([makeQuery(id+"F5.boolean.opBoolean","COPY",EDGE,{"derivedFrom":makeQuery(id+"F5.opExtrude","SWEPT_EDGE",EDGE,{"disambiguationData":[OSD([subQ1,subQ0])]})})])]});}
            var Q39;
            Q39=makeQuery(id+"F1.opExtrude","SWEPT_FACE",FACE,{"disambiguationData":[OSD([sQuery(id+"F0.wireOp",EDGE,"E15.MirrorCS")])]});
            var Q40;
            Q40=makeQuery(id+"F1.opExtrude","SWEPT_FACE",FACE,{"disambiguationData":[OSD([sQuery(id+"F0.wireOp",EDGE,"E14.MirrorCS")])]});
            var Q41;
            {var subQ0=sQuery(id+"F4.wireOp",EDGE,"E21.right");var subQ1=sQuery(id+"F4.wireOp",EDGE,"E21.top");Q41=makeQuery(id+"F22.opFillet","BLEND_FACE",FACE,{"disambiguationData":[OSD([subQ1,subQ0]),TDD([makeQuery(id+"F5.boolean.opBoolean","COPY",EDGE,{"derivedFrom":makeQuery(id+"F5.opExtrude","SWEPT_EDGE",EDGE,{"disambiguationData":[OSD([subQ1,subQ0])]})})])]});}
            var Q42;
            Q42=makeQuery(id+"F1.opExtrude","SWEPT_FACE",FACE,{"disambiguationData":[OSD([sQuery(id+"F0.wireOp",EDGE,"E2")])]});
            var Q43;
            {var subQ0=sQuery(id+"F6.wireOp",EDGE,"E22.right");var subQ1=sQuery(id+"F6.wireOp",EDGE,"E22.top");Q43=makeQuery(id+"F23.opFillet","BLEND_FACE",FACE,{"disambiguationData":[OSD([subQ1,subQ0]),TDD([makeQuery(id+"F7.boolean.opBoolean","COPY",EDGE,{"derivedFrom":makeQuery(id+"F7.opExtrude","SWEPT_EDGE",EDGE,{"disambiguationData":[OSD([subQ1,subQ0])]})})])]});}
            var Q44;
            {var subQ2=sQuery(id+"F2.wireOp",EDGE,"E19.top");var subQ3=makeQuery(id+"F3.boolean.opBoolean","COPY",FACE,{"derivedFrom":makeQuery(id+"F3.opExtrude","SWEPT_FACE",FACE,{"disambiguationData":[OSD([subQ2])]})});var subQ4=sQuery(id+"F10.wireOp",EDGE,"E24.right");var subQ16=sQuery(id+"F2.wireOp",EDGE,"E18.top");Q44=makeQuery(id+"F21.boolean.opBoolean","SPLIT",FACE,{"disambiguationData":[TD([subQ3])],"derivedFrom":makeQuery(id+"F19.boolean.opBoolean","SPLIT",FACE,{"disambiguationData":[TD([subQ3])],"derivedFrom":makeQuery(id+"F17.boolean.opBoolean","SPLIT",FACE,{"disambiguationData":[TD([makeQuery(id+"F3.boolean.opBoolean","COPY",FACE,{"derivedFrom":makeQuery(id+"F3.opExtrude","SWEPT_FACE",FACE,{"disambiguationData":[OSD([subQ16])]})})])],"derivedFrom":makeQuery(id+"F11.boolean.opBoolean","COPY",FACE,{"derivedFrom":makeQuery(id+"F11.opExtrude","SWEPT_FACE",FACE,{"disambiguationData":[OSD([subQ4])]})})})})});}
            var Q45;
            Q45=makeQuery(id+"F19.boolean.opBoolean","COPY",FACE,{"derivedFrom":makeQuery(id+"F19.opExtrude","SWEPT_FACE",FACE,{"disambiguationData":[OSD([sQuery(id+"F18.wireOp",EDGE,"E39")])]})});
            var Q46;
            Q46=makeQuery(id+"F23.opFillet","BLEND_FACE",FACE,{"disambiguationData":[OSD([sQuery(id+"F6.wireOp",EDGE,"E22.top")])]});
            var Q47;
            Q47=makeQuery(id+"F23.opFillet","BLEND_FACE",FACE,{"disambiguationData":[OSD([sQuery(id+"F6.wireOp",EDGE,"E22.left")])]});
            var Q48;
            Q48=makeQuery(id+"F23.opFillet","BLEND_FACE",FACE,{"disambiguationData":[OSD([sQuery(id+"F6.wireOp",EDGE,"E22.right")])]});
            var Q49;
            Q49=makeQuery(id+"F23.opFillet","BLEND_FACE",FACE,{"disambiguationData":[OSD([sQuery(id+"F6.wireOp",EDGE,"E22.bottom")])]});
            var Q50;
            {var subQ0=sQuery(id+"F6.wireOp",EDGE,"E22.right");var subQ1=sQuery(id+"F6.wireOp",EDGE,"E22.bottom");Q50=makeQuery(id+"F23.opFillet","BLEND_FACE",FACE,{"disambiguationData":[OSD([subQ1,subQ0]),TDD([makeQuery(id+"F7.boolean.opBoolean","COPY",EDGE,{"derivedFrom":makeQuery(id+"F7.opExtrude","SWEPT_EDGE",EDGE,{"disambiguationData":[OSD([subQ1,subQ0])]})})])]});}
            var Q51;
            Q51=makeQuery(id+"F3.boolean.opBoolean","COPY",FACE,{"derivedFrom":makeQuery(id+"F3.opExtrude","SWEPT_FACE",FACE,{"disambiguationData":[OSD([sQuery(id+"F2.wireOp",EDGE,"E19.right")])]})});
            var Q52;
            {var subQ0=sQuery(id+"F6.wireOp",EDGE,"E22.right");var subQ1=sQuery(id+"F6.wireOp",EDGE,"E22.top");Q52=makeQuery(id+"F23.opFillet","BLEND_FACE",FACE,{"disambiguationData":[OSD([subQ1,subQ0]),TDD([makeQuery(id+"F7.boolean.opBoolean","COPY",VERTEX,{"derivedFrom":makeQuery(id+"F7.opExtrude","CAP_VERTEX",VERTEX,{"disambiguationData":[OSD([subQ1,subQ0])],"isStart":false})})])]});}
            var Q53;
            {var subQ0=sQuery(id+"F4.wireOp",EDGE,"E21.right");var subQ1=sQuery(id+"F4.wireOp",EDGE,"E21.top");Q53=makeQuery(id+"F22.opFillet","BLEND_FACE",FACE,{"disambiguationData":[OSD([subQ1,subQ0]),TDD([makeQuery(id+"F5.boolean.opBoolean","COPY",VERTEX,{"derivedFrom":makeQuery(id+"F5.opExtrude","CAP_VERTEX",VERTEX,{"disambiguationData":[OSD([subQ1,subQ0])],"isStart":false})})])]});}
            var Q54;
            {var subQ1=sQuery(id+"F2.wireOp",EDGE,"E19.right");var subQ2=sQuery(id+"F2.wireOp",EDGE,"E19.left");var subQ3=sQuery(id+"F2.wireOp",EDGE,"E19.bottom");var subQ5=makeQuery(id+"F3.boolean.opBoolean","COPY",FACE,{"derivedFrom":makeQuery(id+"F3.opExtrude","SWEPT_FACE",FACE,{"disambiguationData":[OSD([subQ3])]})});Q54=makeQuery(id+"F19.boolean.opBoolean","MERGE",FACE,{"derivedFrom":[makeQuery(id+"F11.boolean.opBoolean","SPLIT",FACE,{"disambiguationData":[TD([makeQuery(id+"F3.boolean.opBoolean","COPY",FACE,{"derivedFrom":makeQuery(id+"F3.opExtrude","SWEPT_FACE",FACE,{"disambiguationData":[OSD([subQ2])]})})])],"derivedFrom":subQ5}),makeQuery(id+"F11.boolean.opBoolean","SPLIT",FACE,{"disambiguationData":[TD([makeQuery(id+"F3.boolean.opBoolean","COPY",FACE,{"derivedFrom":makeQuery(id+"F3.opExtrude","SWEPT_FACE",FACE,{"disambiguationData":[OSD([subQ1])]})})])],"derivedFrom":subQ5}),makeQuery(id+"F19.opExtrude","CAP_FACE",FACE,{"disambiguationData":[OSD([sQuery(id+"F18.wireOp",EDGE,"E37"),sQuery(id+"F18.wireOp",EDGE,"E38"),sQuery(id+"F18.wireOp",EDGE,"E39"),sQuery(id+"F18.wireOp",EDGE,"E40"),sQuery(id+"F18.wireOp",EDGE,"E41")])],"isStart":true})]});}
            var Q55;
            Q55=makeQuery(id+"F13.boolean.opBoolean","COPY",FACE,{"derivedFrom":makeQuery(id+"F13.opExtrude","CAP_FACE",FACE,{"disambiguationData":[OSD([sQuery(id+"F12.wireOp",EDGE,"E27")])],"isStart":false})});
            var Q56;
            Q56=makeQuery(id+"F17.boolean.opBoolean","COPY",FACE,{"derivedFrom":makeQuery(id+"F17.opExtrude","SWEPT_FACE",FACE,{"disambiguationData":[OSD([sQuery(id+"F16.wireOp",EDGE,"E32")])]})});
            var Q57;
            Q57=makeQuery(id+"F22.opFillet","BLEND_FACE",FACE,{"disambiguationData":[OSD([sQuery(id+"F4.wireOp",EDGE,"E21.right")])]});
            var Q58;
            Q58=makeQuery(id+"F13.boolean.opBoolean","COPY",FACE,{"derivedFrom":makeQuery(id+"F13.opExtrude","CAP_FACE",FACE,{"disambiguationData":[OSD([sQuery(id+"F12.wireOp",EDGE,"E25")])],"isStart":false})});
            var Q59;
            Q59=makeQuery(id+"F3.boolean.opBoolean","COPY",FACE,{"derivedFrom":makeQuery(id+"F3.opExtrude","SWEPT_FACE",FACE,{"disambiguationData":[OSD([sQuery(id+"F2.wireOp",EDGE,"E20.right")])]})});
            var Q60;
            Q60=makeQuery(id+"F21.boolean.opBoolean","COPY",FACE,{"derivedFrom":makeQuery(id+"F21.opExtrude","SWEPT_FACE",FACE,{"disambiguationData":[OSD([sQuery(id+"F20.wireOp",EDGE,"E45")])]})});
            var Q61;
            {var subQ2=sQuery(id+"F10.wireOp",EDGE,"E24.left");var subQ5=sQuery(id+"F2.wireOp",EDGE,"E18.top");var subQ6=sQuery(id+"F10.wireOp",EDGE,"E24.bottom");Q61=makeQuery(id+"F21.boolean.opBoolean","SPLIT",FACE,{"disambiguationData":[TD([makeQuery(id+"F3.boolean.opBoolean","COPY",FACE,{"derivedFrom":makeQuery(id+"F3.opExtrude","SWEPT_FACE",FACE,{"disambiguationData":[OSD([sQuery(id+"F2.wireOp",EDGE,"E20.top")])]})})])],"derivedFrom":makeQuery(id+"F19.boolean.opBoolean","SPLIT",FACE,{"disambiguationData":[TD([makeQuery(id+"F3.boolean.opBoolean","COPY",FACE,{"derivedFrom":makeQuery(id+"F3.opExtrude","SWEPT_FACE",FACE,{"disambiguationData":[OSD([sQuery(id+"F2.wireOp",EDGE,"E19.top")])]})})])],"derivedFrom":makeQuery(id+"F17.boolean.opBoolean","SPLIT",FACE,{"disambiguationData":[TD([makeQuery(id+"F3.boolean.opBoolean","COPY",FACE,{"derivedFrom":makeQuery(id+"F3.opExtrude","SWEPT_FACE",FACE,{"disambiguationData":[OSD([subQ5])]})})])],"derivedFrom":makeQuery(id+"F11.boolean.opBoolean","COPY",FACE,{"derivedFrom":makeQuery(id+"F11.opExtrude","SWEPT_FACE",FACE,{"disambiguationData":[OSD([subQ6]),TDD([makeQuery(id+"F10.imprint","IMPRINT",EDGE,{"disambiguationData":[TD([[makeQuery(id+"F10.imprint","INTERSECT",VERTEX,{"derivedFrom":[subQ6,subQ2]}),-1.0]])],"derivedFrom":subQ6})])]})})})})});}
            var Q62;
            {var subQ2=sQuery(id+"F10.wireOp",EDGE,"E24.left");var subQ4=makeQuery(id+"F3.boolean.opBoolean","COPY",FACE,{"derivedFrom":makeQuery(id+"F3.opExtrude","SWEPT_FACE",FACE,{"disambiguationData":[OSD([sQuery(id+"F2.wireOp",EDGE,"E19.top")])]})});var subQ7=sQuery(id+"F2.wireOp",EDGE,"E18.top");var subQ8=sQuery(id+"F10.wireOp",EDGE,"E24.bottom");Q62=makeQuery(id+"F21.boolean.opBoolean","SPLIT",FACE,{"disambiguationData":[TD([subQ4])],"derivedFrom":makeQuery(id+"F19.boolean.opBoolean","SPLIT",FACE,{"disambiguationData":[TD([subQ4])],"derivedFrom":makeQuery(id+"F17.boolean.opBoolean","SPLIT",FACE,{"disambiguationData":[TD([makeQuery(id+"F3.boolean.opBoolean","COPY",FACE,{"derivedFrom":makeQuery(id+"F3.opExtrude","SWEPT_FACE",FACE,{"disambiguationData":[OSD([subQ7])]})})])],"derivedFrom":makeQuery(id+"F11.boolean.opBoolean","COPY",FACE,{"derivedFrom":makeQuery(id+"F11.opExtrude","SWEPT_FACE",FACE,{"disambiguationData":[OSD([subQ8]),TDD([makeQuery(id+"F10.imprint","IMPRINT",EDGE,{"disambiguationData":[TD([[makeQuery(id+"F10.imprint","INTERSECT",VERTEX,{"derivedFrom":[subQ8,subQ2]}),-1.0]])],"derivedFrom":subQ8})])]})})})})});}
            var Q63;
            Q63=makeQuery(id+"F17.boolean.opBoolean","COPY",FACE,{"derivedFrom":makeQuery(id+"F17.opExtrude","SWEPT_FACE",FACE,{"disambiguationData":[OSD([sQuery(id+"F16.wireOp",EDGE,"E33")])]})});
            var Q64;
            Q64=makeQuery(id+"F13.boolean.opBoolean","COPY",FACE,{"derivedFrom":makeQuery(id+"F13.opExtrude","CAP_FACE",FACE,{"disambiguationData":[OSD([sQuery(id+"F12.wireOp",EDGE,"E26")])],"isStart":false})});
            var Q65;
            Q65=makeQuery(id+"F1.opExtrude","SWEPT_FACE",FACE,{"disambiguationData":[OSD([sQuery(id+"F0.wireOp",EDGE,"E16.MirrorCS")])]});
            var Q66;
            Q66=makeQuery(id+"F15.boolean.opBoolean","COPY",FACE,{"derivedFrom":makeQuery(id+"F15.opExtrude","CAP_FACE",FACE,{"disambiguationData":[OSD([sQuery(id+"F14.wireOp",EDGE,"E30")])],"isStart":false})});
            var Q67;
            Q67=makeQuery(id+"F15.boolean.opBoolean","COPY",FACE,{"derivedFrom":makeQuery(id+"F15.opExtrude","SWEPT_FACE",FACE,{"disambiguationData":[OSD([sQuery(id+"F14.wireOp",EDGE,"E29")])]})});
            var Q68;
            {var subQ0=sQuery(id+"F10.wireOp",EDGE,"E24.right");var subQ2=sQuery(id+"F10.wireOp",EDGE,"E24.bottom");Q68=makeQuery(id+"F17.boolean.opBoolean","SPLIT",FACE,{"disambiguationData":[TD([makeQuery(id+"F3.boolean.opBoolean","COPY",FACE,{"derivedFrom":makeQuery(id+"F3.opExtrude","SWEPT_FACE",FACE,{"disambiguationData":[OSD([sQuery(id+"F2.wireOp",EDGE,"E18.bottom")])]})})])],"derivedFrom":makeQuery(id+"F11.boolean.opBoolean","COPY",FACE,{"derivedFrom":makeQuery(id+"F11.opExtrude","SWEPT_FACE",FACE,{"disambiguationData":[OSD([subQ2]),TDD([makeQuery(id+"F10.imprint","IMPRINT",EDGE,{"disambiguationData":[TD([[makeQuery(id+"F10.imprint","INTERSECT",VERTEX,{"derivedFrom":[subQ2,subQ0]}),1.0]])],"derivedFrom":subQ2})])]})})});}
            var Q69;
            {var subQ0=sQuery(id+"F10.wireOp",EDGE,"E24.right");var subQ5=sQuery(id+"F2.wireOp",EDGE,"E18.top");var subQ6=sQuery(id+"F10.wireOp",EDGE,"E24.bottom");Q69=makeQuery(id+"F21.boolean.opBoolean","SPLIT",FACE,{"disambiguationData":[TD([makeQuery(id+"F3.boolean.opBoolean","COPY",FACE,{"derivedFrom":makeQuery(id+"F3.opExtrude","SWEPT_FACE",FACE,{"disambiguationData":[OSD([sQuery(id+"F2.wireOp",EDGE,"E20.top")])]})})])],"derivedFrom":makeQuery(id+"F19.boolean.opBoolean","SPLIT",FACE,{"disambiguationData":[TD([makeQuery(id+"F3.boolean.opBoolean","COPY",FACE,{"derivedFrom":makeQuery(id+"F3.opExtrude","SWEPT_FACE",FACE,{"disambiguationData":[OSD([sQuery(id+"F2.wireOp",EDGE,"E19.top")])]})})])],"derivedFrom":makeQuery(id+"F17.boolean.opBoolean","SPLIT",FACE,{"disambiguationData":[TD([makeQuery(id+"F3.boolean.opBoolean","COPY",FACE,{"derivedFrom":makeQuery(id+"F3.opExtrude","SWEPT_FACE",FACE,{"disambiguationData":[OSD([subQ5])]})})])],"derivedFrom":makeQuery(id+"F11.boolean.opBoolean","COPY",FACE,{"derivedFrom":makeQuery(id+"F11.opExtrude","SWEPT_FACE",FACE,{"disambiguationData":[OSD([subQ6]),TDD([makeQuery(id+"F10.imprint","IMPRINT",EDGE,{"disambiguationData":[TD([[makeQuery(id+"F10.imprint","INTERSECT",VERTEX,{"derivedFrom":[subQ6,subQ0]}),1.0]])],"derivedFrom":subQ6})])]})})})})});}
            var Q70;
            {var subQ0=sQuery(id+"F4.wireOp",EDGE,"E21.left");var subQ1=sQuery(id+"F4.wireOp",EDGE,"E21.bottom");Q70=makeQuery(id+"F22.opFillet","BLEND_FACE",FACE,{"disambiguationData":[OSD([subQ1,subQ0]),TDD([makeQuery(id+"F5.boolean.opBoolean","COPY",VERTEX,{"derivedFrom":makeQuery(id+"F5.opExtrude","CAP_VERTEX",VERTEX,{"disambiguationData":[OSD([subQ1,subQ0])],"isStart":false})})])]});}
            var Q71;
            {var subQ0=sQuery(id+"F10.wireOp",EDGE,"E24.right");var subQ2=makeQuery(id+"F3.boolean.opBoolean","COPY",FACE,{"derivedFrom":makeQuery(id+"F3.opExtrude","SWEPT_FACE",FACE,{"disambiguationData":[OSD([sQuery(id+"F2.wireOp",EDGE,"E19.top")])]})});var subQ7=sQuery(id+"F2.wireOp",EDGE,"E18.top");var subQ8=sQuery(id+"F10.wireOp",EDGE,"E24.bottom");Q71=makeQuery(id+"F21.boolean.opBoolean","SPLIT",FACE,{"disambiguationData":[TD([subQ2])],"derivedFrom":makeQuery(id+"F19.boolean.opBoolean","SPLIT",FACE,{"disambiguationData":[TD([subQ2])],"derivedFrom":makeQuery(id+"F17.boolean.opBoolean","SPLIT",FACE,{"disambiguationData":[TD([makeQuery(id+"F3.boolean.opBoolean","COPY",FACE,{"derivedFrom":makeQuery(id+"F3.opExtrude","SWEPT_FACE",FACE,{"disambiguationData":[OSD([subQ7])]})})])],"derivedFrom":makeQuery(id+"F11.boolean.opBoolean","COPY",FACE,{"derivedFrom":makeQuery(id+"F11.opExtrude","SWEPT_FACE",FACE,{"disambiguationData":[OSD([subQ8]),TDD([makeQuery(id+"F10.imprint","IMPRINT",EDGE,{"disambiguationData":[TD([[makeQuery(id+"F10.imprint","INTERSECT",VERTEX,{"derivedFrom":[subQ8,subQ0]}),1.0]])],"derivedFrom":subQ8})])]})})})})});}
            var Q72;
            Q72=makeQuery(id+"F15.boolean.opBoolean","COPY",FACE,{"derivedFrom":makeQuery(id+"F15.opExtrude","SWEPT_FACE",FACE,{"disambiguationData":[OSD([sQuery(id+"F14.wireOp",EDGE,"E30")])]})});
            var Q73;
            Q73=makeQuery(id+"F13.boolean.opBoolean","COPY",FACE,{"derivedFrom":makeQuery(id+"F13.opExtrude","SWEPT_FACE",FACE,{"disambiguationData":[OSD([sQuery(id+"F12.wireOp",EDGE,"E25")])]})});
            var Q74;
            {var subQ1=sQuery(id+"F2.wireOp",EDGE,"E20.right");var subQ2=sQuery(id+"F2.wireOp",EDGE,"E20.left");var subQ3=sQuery(id+"F2.wireOp",EDGE,"E20.bottom");var subQ5=makeQuery(id+"F3.boolean.opBoolean","COPY",FACE,{"derivedFrom":makeQuery(id+"F3.opExtrude","SWEPT_FACE",FACE,{"disambiguationData":[OSD([subQ3])]})});Q74=makeQuery(id+"F21.boolean.opBoolean","MERGE",FACE,{"derivedFrom":[makeQuery(id+"F11.boolean.opBoolean","SPLIT",FACE,{"disambiguationData":[TD([makeQuery(id+"F3.boolean.opBoolean","COPY",FACE,{"derivedFrom":makeQuery(id+"F3.opExtrude","SWEPT_FACE",FACE,{"disambiguationData":[OSD([subQ2])]})})])],"derivedFrom":subQ5}),makeQuery(id+"F11.boolean.opBoolean","SPLIT",FACE,{"disambiguationData":[TD([makeQuery(id+"F3.boolean.opBoolean","COPY",FACE,{"derivedFrom":makeQuery(id+"F3.opExtrude","SWEPT_FACE",FACE,{"disambiguationData":[OSD([subQ1])]})})])],"derivedFrom":subQ5}),makeQuery(id+"F21.opExtrude","CAP_FACE",FACE,{"disambiguationData":[OSD([sQuery(id+"F20.wireOp",EDGE,"E43"),sQuery(id+"F20.wireOp",EDGE,"E45"),sQuery(id+"F20.wireOp",EDGE,"E46"),sQuery(id+"F20.wireOp",EDGE,"E47"),sQuery(id+"F20.wireOp",EDGE,"E48")])],"isStart":true})]});}
            var Q75;
            {var subQ0=sQuery(id+"F10.wireOp",EDGE,"E24.right");var subQ1=sQuery(id+"F2.wireOp",EDGE,"E18.top");var subQ3=sQuery(id+"F2.wireOp",EDGE,"E18.right");var subQ4=sQuery(id+"F2.wireOp",EDGE,"E18.left");var subQ6=makeQuery(id+"F3.boolean.opBoolean","COPY",FACE,{"derivedFrom":makeQuery(id+"F3.opExtrude","SWEPT_FACE",FACE,{"disambiguationData":[OSD([subQ1])]})});Q75=makeQuery(id+"F17.boolean.opBoolean","MERGE",FACE,{"derivedFrom":[makeQuery(id+"F11.boolean.opBoolean","SPLIT",FACE,{"disambiguationData":[TD([makeQuery(id+"F3.boolean.opBoolean","COPY",FACE,{"derivedFrom":makeQuery(id+"F3.opExtrude","SWEPT_FACE",FACE,{"disambiguationData":[OSD([subQ4])]})})])],"derivedFrom":subQ6}),makeQuery(id+"F11.boolean.opBoolean","SPLIT",FACE,{"disambiguationData":[TD([makeQuery(id+"F3.boolean.opBoolean","COPY",FACE,{"derivedFrom":makeQuery(id+"F3.opExtrude","SWEPT_FACE",FACE,{"disambiguationData":[OSD([subQ3])]})})])],"derivedFrom":subQ6}),makeQuery(id+"F17.opExtrude","CAP_FACE",FACE,{"disambiguationData":[OSD([subQ1,subQ0,sQuery(id+"F16.wireOp",EDGE,"E31"),sQuery(id+"F16.wireOp",EDGE,"E32"),sQuery(id+"F16.wireOp",EDGE,"E33"),sQuery(id+"F16.wireOp",EDGE,"E34"),sQuery(id+"F16.wireOp",EDGE,"E35")])],"isStart":true})]});}
            var Q76;
            Q76=makeQuery(id+"F21.boolean.opBoolean","COPY",FACE,{"derivedFrom":makeQuery(id+"F21.opExtrude","SWEPT_FACE",FACE,{"disambiguationData":[OSD([sQuery(id+"F20.wireOp",EDGE,"E48")])]})});
            var Q77;
            Q77=makeQuery(id+"F3.boolean.opBoolean","COPY",FACE,{"derivedFrom":makeQuery(id+"F3.opExtrude","SWEPT_FACE",FACE,{"disambiguationData":[OSD([sQuery(id+"F2.wireOp",EDGE,"E18.right")])]})});
            var Q78;
            {var subQ0=sQuery(id+"F10.wireOp",EDGE,"E24.right");var subQ1=sQuery(id+"F2.wireOp",EDGE,"E18.top");var subQ3=sQuery(id+"F2.wireOp",EDGE,"E18.right");var subQ4=sQuery(id+"F2.wireOp",EDGE,"E18.left");var subQ5=sQuery(id+"F2.wireOp",EDGE,"E18.bottom");var subQ7=makeQuery(id+"F3.boolean.opBoolean","COPY",FACE,{"derivedFrom":makeQuery(id+"F3.opExtrude","SWEPT_FACE",FACE,{"disambiguationData":[OSD([subQ5])]})});Q78=makeQuery(id+"F17.boolean.opBoolean","MERGE",FACE,{"derivedFrom":[makeQuery(id+"F11.boolean.opBoolean","SPLIT",FACE,{"disambiguationData":[TD([makeQuery(id+"F3.boolean.opBoolean","COPY",FACE,{"derivedFrom":makeQuery(id+"F3.opExtrude","SWEPT_FACE",FACE,{"disambiguationData":[OSD([subQ4])]})})])],"derivedFrom":subQ7}),makeQuery(id+"F11.boolean.opBoolean","SPLIT",FACE,{"disambiguationData":[TD([makeQuery(id+"F3.boolean.opBoolean","COPY",FACE,{"derivedFrom":makeQuery(id+"F3.opExtrude","SWEPT_FACE",FACE,{"disambiguationData":[OSD([subQ3])]})})])],"derivedFrom":subQ7}),makeQuery(id+"F17.opExtrude","CAP_FACE",FACE,{"disambiguationData":[OSD([subQ1,subQ0,sQuery(id+"F16.wireOp",EDGE,"E31"),sQuery(id+"F16.wireOp",EDGE,"E32"),sQuery(id+"F16.wireOp",EDGE,"E33"),sQuery(id+"F16.wireOp",EDGE,"E34"),sQuery(id+"F16.wireOp",EDGE,"E35")])],"isStart":false})]});}
            var Q79;
            {var subQ0=sQuery(id+"F6.wireOp",EDGE,"E22.right");var subQ1=sQuery(id+"F6.wireOp",EDGE,"E22.bottom");Q79=makeQuery(id+"F23.opFillet","BLEND_FACE",FACE,{"disambiguationData":[OSD([subQ1,subQ0]),TDD([makeQuery(id+"F7.boolean.opBoolean","COPY",VERTEX,{"derivedFrom":makeQuery(id+"F7.opExtrude","CAP_VERTEX",VERTEX,{"disambiguationData":[OSD([subQ1,subQ0])],"isStart":false})})])]});}
            var Q80;
            {var subQ0=sQuery(id+"F6.wireOp",EDGE,"E22.left");var subQ1=sQuery(id+"F6.wireOp",EDGE,"E22.top");Q80=makeQuery(id+"F23.opFillet","BLEND_FACE",FACE,{"disambiguationData":[OSD([subQ1,subQ0]),TDD([makeQuery(id+"F7.boolean.opBoolean","COPY",EDGE,{"derivedFrom":makeQuery(id+"F7.opExtrude","SWEPT_EDGE",EDGE,{"disambiguationData":[OSD([subQ1,subQ0])]})})])]});}
            var Q81;
            {var subQ0=sQuery(id+"F10.wireOp",EDGE,"E24.left");var subQ6=sQuery(id+"F2.wireOp",EDGE,"E20.top");var subQ7=makeQuery(id+"F3.boolean.opBoolean","COPY",FACE,{"derivedFrom":makeQuery(id+"F3.opExtrude","SWEPT_FACE",FACE,{"disambiguationData":[OSD([subQ6])]})});var subQ9=sQuery(id+"F2.wireOp",EDGE,"E19.top");var subQ10=makeQuery(id+"F3.boolean.opBoolean","COPY",FACE,{"derivedFrom":makeQuery(id+"F3.opExtrude","SWEPT_FACE",FACE,{"disambiguationData":[OSD([subQ9])]})});var subQ15=sQuery(id+"F2.wireOp",EDGE,"E18.top");Q81=makeQuery(id+"F21.boolean.opBoolean","SPLIT",FACE,{"disambiguationData":[TD([subQ7])],"derivedFrom":makeQuery(id+"F19.boolean.opBoolean","SPLIT",FACE,{"disambiguationData":[TD([subQ10])],"derivedFrom":makeQuery(id+"F17.boolean.opBoolean","SPLIT",FACE,{"disambiguationData":[TD([makeQuery(id+"F3.boolean.opBoolean","COPY",FACE,{"derivedFrom":makeQuery(id+"F3.opExtrude","SWEPT_FACE",FACE,{"disambiguationData":[OSD([subQ15])]})})])],"derivedFrom":makeQuery(id+"F11.boolean.opBoolean","COPY",FACE,{"derivedFrom":makeQuery(id+"F11.opExtrude","SWEPT_FACE",FACE,{"disambiguationData":[OSD([subQ0])]})})})})});}
            var Q82;
            Q82=makeQuery(id+"F7.boolean.opBoolean","COPY",FACE,{"derivedFrom":makeQuery(id+"F7.opExtrude","CAP_FACE",FACE,{"disambiguationData":[OSD([sQuery(id+"F6.wireOp",EDGE,"E22.bottom"),sQuery(id+"F6.wireOp",EDGE,"E22.top"),sQuery(id+"F6.wireOp",EDGE,"E22.left"),sQuery(id+"F6.wireOp",EDGE,"E22.right")])],"isStart":false})});
            var Q83;
            Q83=makeQuery(id+"F19.boolean.opBoolean","COPY",FACE,{"derivedFrom":makeQuery(id+"F19.opExtrude","SWEPT_FACE",FACE,{"disambiguationData":[OSD([sQuery(id+"F18.wireOp",EDGE,"E41")])]})});
            var Q84;
            {var subQ0=sQuery(id+"F10.wireOp",EDGE,"E24.left");var subQ2=sQuery(id+"F10.wireOp",EDGE,"E24.bottom");Q84=makeQuery(id+"F17.boolean.opBoolean","SPLIT",FACE,{"disambiguationData":[TD([makeQuery(id+"F3.boolean.opBoolean","COPY",FACE,{"derivedFrom":makeQuery(id+"F3.opExtrude","SWEPT_FACE",FACE,{"disambiguationData":[OSD([sQuery(id+"F2.wireOp",EDGE,"E18.bottom")])]})})])],"derivedFrom":makeQuery(id+"F11.boolean.opBoolean","COPY",FACE,{"derivedFrom":makeQuery(id+"F11.opExtrude","SWEPT_FACE",FACE,{"disambiguationData":[OSD([subQ2]),TDD([makeQuery(id+"F10.imprint","IMPRINT",EDGE,{"disambiguationData":[TD([[makeQuery(id+"F10.imprint","INTERSECT",VERTEX,{"derivedFrom":[subQ2,subQ0]}),-1.0]])],"derivedFrom":subQ2})])]})})});}
            var Q85;
            Q85=makeQuery(id+"F15.boolean.opBoolean","COPY",FACE,{"derivedFrom":makeQuery(id+"F15.opExtrude","CAP_FACE",FACE,{"disambiguationData":[OSD([sQuery(id+"F14.wireOp",EDGE,"E29")])],"isStart":false})});
            var Q86;
            Q86=makeQuery(id+"F15.boolean.opBoolean","COPY",FACE,{"derivedFrom":makeQuery(id+"F15.opExtrude","SWEPT_FACE",FACE,{"disambiguationData":[OSD([sQuery(id+"F14.wireOp",EDGE,"E28")])]})});
            var Q87;
            Q87=makeQuery(id+"F17.boolean.opBoolean","COPY",FACE,{"derivedFrom":makeQuery(id+"F17.opExtrude","SWEPT_FACE",FACE,{"disambiguationData":[OSD([sQuery(id+"F16.wireOp",EDGE,"E31")])]})});
            var Q88;
            Q88=makeQuery(id+"F22.opFillet","BLEND_FACE",FACE,{"disambiguationData":[OSD([sQuery(id+"F4.wireOp",EDGE,"E21.top")])]});
            var Q89;
            {var subQ2=sQuery(id+"F8.wireOp",EDGE,"E23");Q89=makeQuery(id+"F17.boolean.opBoolean","SPLIT",FACE,{"disambiguationData":[TD([makeQuery(id+"F3.boolean.opBoolean","COPY",FACE,{"derivedFrom":makeQuery(id+"F3.opExtrude","SWEPT_FACE",FACE,{"disambiguationData":[OSD([sQuery(id+"F2.wireOp",EDGE,"E18.bottom")])]})})])],"derivedFrom":makeQuery(id+"F9.boolean.opBoolean","COPY",FACE,{"derivedFrom":makeQuery(id+"F9.opExtrude","SWEPT_FACE",FACE,{"disambiguationData":[OSD([subQ2])]})})});}
            var Q90;
            {var subQ0=sQuery(id+"F10.wireOp",EDGE,"E24.right");Q90=makeQuery(id+"F17.boolean.opBoolean","SPLIT",FACE,{"disambiguationData":[TD([makeQuery(id+"F3.boolean.opBoolean","COPY",FACE,{"derivedFrom":makeQuery(id+"F3.opExtrude","SWEPT_FACE",FACE,{"disambiguationData":[OSD([sQuery(id+"F2.wireOp",EDGE,"E18.bottom")])]})})])],"derivedFrom":makeQuery(id+"F11.boolean.opBoolean","COPY",FACE,{"derivedFrom":makeQuery(id+"F11.opExtrude","SWEPT_FACE",FACE,{"disambiguationData":[OSD([subQ0])]})})});}
            var Q91;
            {var subQ0=sQuery(id+"F4.wireOp",EDGE,"E21.left");var subQ1=sQuery(id+"F4.wireOp",EDGE,"E21.top");Q91=makeQuery(id+"F22.opFillet","BLEND_FACE",FACE,{"disambiguationData":[OSD([subQ1,subQ0]),TDD([makeQuery(id+"F5.boolean.opBoolean","COPY",VERTEX,{"derivedFrom":makeQuery(id+"F5.opExtrude","CAP_VERTEX",VERTEX,{"disambiguationData":[OSD([subQ1,subQ0])],"isStart":false})})])]});}
            var Q92;
            {var subQ2=sQuery(id+"F8.wireOp",EDGE,"E23");var subQ6=sQuery(id+"F2.wireOp",EDGE,"E18.top");var subQ7=makeQuery(id+"F3.boolean.opBoolean","COPY",FACE,{"derivedFrom":makeQuery(id+"F3.opExtrude","SWEPT_FACE",FACE,{"disambiguationData":[OSD([subQ6])]})});Q92=makeQuery(id+"F19.boolean.opBoolean","SPLIT",FACE,{"disambiguationData":[TD([subQ7])],"derivedFrom":makeQuery(id+"F17.boolean.opBoolean","SPLIT",FACE,{"disambiguationData":[TD([subQ7])],"derivedFrom":makeQuery(id+"F9.boolean.opBoolean","COPY",FACE,{"derivedFrom":makeQuery(id+"F9.opExtrude","SWEPT_FACE",FACE,{"disambiguationData":[OSD([subQ2])]})})})});}
            var Q93;
            Q93=makeQuery(id+"F21.boolean.opBoolean","COPY",FACE,{"derivedFrom":makeQuery(id+"F21.opExtrude","SWEPT_FACE",FACE,{"disambiguationData":[OSD([sQuery(id+"F20.wireOp",EDGE,"E47")])]})});
            var Q94;
            {var subQ0=sQuery(id+"F6.wireOp",EDGE,"E22.left");var subQ1=sQuery(id+"F6.wireOp",EDGE,"E22.top");Q94=makeQuery(id+"F23.opFillet","BLEND_FACE",FACE,{"disambiguationData":[OSD([subQ1,subQ0]),TDD([makeQuery(id+"F7.boolean.opBoolean","COPY",VERTEX,{"derivedFrom":makeQuery(id+"F7.opExtrude","CAP_VERTEX",VERTEX,{"disambiguationData":[OSD([subQ1,subQ0])],"isStart":false})})])]});}
            var Q95;
            {var subQ2=sQuery(id+"F2.wireOp",EDGE,"E18.top");var subQ3=makeQuery(id+"F3.boolean.opBoolean","COPY",FACE,{"derivedFrom":makeQuery(id+"F3.opExtrude","SWEPT_FACE",FACE,{"disambiguationData":[OSD([subQ2])]})});var subQ4=sQuery(id+"F10.wireOp",EDGE,"E24.right");Q95=makeQuery(id+"F19.boolean.opBoolean","SPLIT",FACE,{"disambiguationData":[TD([subQ3])],"derivedFrom":makeQuery(id+"F17.boolean.opBoolean","SPLIT",FACE,{"disambiguationData":[TD([subQ3])],"derivedFrom":makeQuery(id+"F11.boolean.opBoolean","COPY",FACE,{"derivedFrom":makeQuery(id+"F11.opExtrude","SWEPT_FACE",FACE,{"disambiguationData":[OSD([subQ4])]})})})});}
            var Q96;
            Q96=makeQuery(id+"F3.boolean.opBoolean","COPY",FACE,{"derivedFrom":makeQuery(id+"F3.opExtrude","SWEPT_FACE",FACE,{"disambiguationData":[OSD([sQuery(id+"F2.wireOp",EDGE,"E19.left")])]})});
            var Q97;
            Q97=makeQuery(id+"F3.boolean.opBoolean","COPY",FACE,{"derivedFrom":makeQuery(id+"F3.opExtrude","SWEPT_FACE",FACE,{"disambiguationData":[OSD([sQuery(id+"F2.wireOp",EDGE,"E20.left")])]})});
            var Q98;
            {var subQ0=sQuery(id+"F10.wireOp",EDGE,"E24.left");var subQ5=sQuery(id+"F2.wireOp",EDGE,"E19.top");var subQ6=makeQuery(id+"F3.boolean.opBoolean","COPY",FACE,{"derivedFrom":makeQuery(id+"F3.opExtrude","SWEPT_FACE",FACE,{"disambiguationData":[OSD([subQ5])]})});var subQ16=sQuery(id+"F2.wireOp",EDGE,"E18.top");Q98=makeQuery(id+"F21.boolean.opBoolean","SPLIT",FACE,{"disambiguationData":[TD([subQ6])],"derivedFrom":makeQuery(id+"F19.boolean.opBoolean","SPLIT",FACE,{"disambiguationData":[TD([subQ6])],"derivedFrom":makeQuery(id+"F17.boolean.opBoolean","SPLIT",FACE,{"disambiguationData":[TD([makeQuery(id+"F3.boolean.opBoolean","COPY",FACE,{"derivedFrom":makeQuery(id+"F3.opExtrude","SWEPT_FACE",FACE,{"disambiguationData":[OSD([subQ16])]})})])],"derivedFrom":makeQuery(id+"F11.boolean.opBoolean","COPY",FACE,{"derivedFrom":makeQuery(id+"F11.opExtrude","SWEPT_FACE",FACE,{"disambiguationData":[OSD([subQ0])]})})})})});}
            var Q99;
            {var subQ0=sQuery(id+"F6.wireOp",EDGE,"E22.left");var subQ1=sQuery(id+"F6.wireOp",EDGE,"E22.bottom");Q99=makeQuery(id+"F23.opFillet","BLEND_FACE",FACE,{"disambiguationData":[OSD([subQ1,subQ0]),TDD([makeQuery(id+"F7.boolean.opBoolean","COPY",VERTEX,{"derivedFrom":makeQuery(id+"F7.opExtrude","CAP_VERTEX",VERTEX,{"disambiguationData":[OSD([subQ1,subQ0])],"isStart":false})})])]});}
            var Q100;
            {var subQ0=sQuery(id+"F10.wireOp",EDGE,"E24.left");var subQ5=sQuery(id+"F2.wireOp",EDGE,"E18.top");var subQ6=makeQuery(id+"F3.boolean.opBoolean","COPY",FACE,{"derivedFrom":makeQuery(id+"F3.opExtrude","SWEPT_FACE",FACE,{"disambiguationData":[OSD([subQ5])]})});Q100=makeQuery(id+"F19.boolean.opBoolean","SPLIT",FACE,{"disambiguationData":[TD([subQ6])],"derivedFrom":makeQuery(id+"F17.boolean.opBoolean","SPLIT",FACE,{"disambiguationData":[TD([subQ6])],"derivedFrom":makeQuery(id+"F11.boolean.opBoolean","COPY",FACE,{"derivedFrom":makeQuery(id+"F11.opExtrude","SWEPT_FACE",FACE,{"disambiguationData":[OSD([subQ0])]})})})});}
            var Q101;
            Q101=makeQuery(id+"F17.boolean.opBoolean","COPY",FACE,{"derivedFrom":makeQuery(id+"F17.opExtrude","SWEPT_FACE",FACE,{"disambiguationData":[OSD([sQuery(id+"F16.wireOp",EDGE,"E34")])]})});
            var Q102;
            Q102=makeQuery(id+"F3.boolean.opBoolean","COPY",FACE,{"derivedFrom":makeQuery(id+"F3.opExtrude","SWEPT_FACE",FACE,{"disambiguationData":[OSD([sQuery(id+"F2.wireOp",EDGE,"E18.left")])]})});
            var Q103;
            Q103=makeQuery(id+"F15.boolean.opBoolean","COPY",FACE,{"derivedFrom":makeQuery(id+"F15.opExtrude","CAP_FACE",FACE,{"disambiguationData":[OSD([sQuery(id+"F14.wireOp",EDGE,"E28")])],"isStart":false})});
            var Q104;
            {var subQ0=sQuery(id+"F10.wireOp",EDGE,"E24.left");var subQ4=sQuery(id+"F2.wireOp",EDGE,"E18.top");var subQ5=makeQuery(id+"F3.boolean.opBoolean","COPY",FACE,{"derivedFrom":makeQuery(id+"F3.opExtrude","SWEPT_FACE",FACE,{"disambiguationData":[OSD([subQ4])]})});var subQ7=sQuery(id+"F10.wireOp",EDGE,"E24.bottom");Q104=makeQuery(id+"F19.boolean.opBoolean","SPLIT",FACE,{"disambiguationData":[TD([subQ5])],"derivedFrom":makeQuery(id+"F17.boolean.opBoolean","SPLIT",FACE,{"disambiguationData":[TD([subQ5])],"derivedFrom":makeQuery(id+"F11.boolean.opBoolean","COPY",FACE,{"derivedFrom":makeQuery(id+"F11.opExtrude","SWEPT_FACE",FACE,{"disambiguationData":[OSD([subQ7]),TDD([makeQuery(id+"F10.imprint","IMPRINT",EDGE,{"disambiguationData":[TD([[makeQuery(id+"F10.imprint","INTERSECT",VERTEX,{"derivedFrom":[subQ7,subQ0]}),-1.0]])],"derivedFrom":subQ7})])]})})})});}
            var Q105;
            Q105=makeQuery(id+"F19.boolean.opBoolean","COPY",FACE,{"derivedFrom":makeQuery(id+"F19.opExtrude","SWEPT_FACE",FACE,{"disambiguationData":[OSD([sQuery(id+"F18.wireOp",EDGE,"E38")])]})});
            var Q106;
            {var subQ0=sQuery(id+"F10.wireOp",EDGE,"E24.right");var subQ4=sQuery(id+"F2.wireOp",EDGE,"E18.top");var subQ5=makeQuery(id+"F3.boolean.opBoolean","COPY",FACE,{"derivedFrom":makeQuery(id+"F3.opExtrude","SWEPT_FACE",FACE,{"disambiguationData":[OSD([subQ4])]})});var subQ7=sQuery(id+"F10.wireOp",EDGE,"E24.bottom");Q106=makeQuery(id+"F19.boolean.opBoolean","SPLIT",FACE,{"disambiguationData":[TD([subQ5])],"derivedFrom":makeQuery(id+"F17.boolean.opBoolean","SPLIT",FACE,{"disambiguationData":[TD([subQ5])],"derivedFrom":makeQuery(id+"F11.boolean.opBoolean","COPY",FACE,{"derivedFrom":makeQuery(id+"F11.opExtrude","SWEPT_FACE",FACE,{"disambiguationData":[OSD([subQ7]),TDD([makeQuery(id+"F10.imprint","IMPRINT",EDGE,{"disambiguationData":[TD([[makeQuery(id+"F10.imprint","INTERSECT",VERTEX,{"derivedFrom":[subQ7,subQ0]}),1.0]])],"derivedFrom":subQ7})])]})})})});}
            var Q107;
            {var subQ0=sQuery(id+"F4.wireOp",EDGE,"E21.right");var subQ1=sQuery(id+"F4.wireOp",EDGE,"E21.bottom");Q107=makeQuery(id+"F22.opFillet","BLEND_FACE",FACE,{"disambiguationData":[OSD([subQ1,subQ0]),TDD([makeQuery(id+"F5.boolean.opBoolean","COPY",VERTEX,{"derivedFrom":makeQuery(id+"F5.opExtrude","CAP_VERTEX",VERTEX,{"disambiguationData":[OSD([subQ1,subQ0])],"isStart":false})})])]});}
            var Q108;
            Q108=makeQuery(id+"F1.opExtrude","SWEPT_BODY",BODY,{"disambiguationData":[OSD([sQuery(id+"F0.wireOp",EDGE,"E2"),sQuery(id+"F0.wireOp",EDGE,"E3"),sQuery(id+"F0.wireOp",EDGE,"E4"),sQuery(id+"F0.wireOp",EDGE,"E5"),sQuery(id+"F0.wireOp",EDGE,"E6"),sQuery(id+"F0.wireOp",EDGE,"E7"),sQuery(id+"F0.wireOp",EDGE,"E8"),sQuery(id+"F0.wireOp",EDGE,"E9"),sQuery(id+"F0.wireOp",EDGE,"E10.MirrorCS"),sQuery(id+"F0.wireOp",EDGE,"E11.MirrorCS"),sQuery(id+"F0.wireOp",EDGE,"E12.MirrorCS"),sQuery(id+"F0.wireOp",EDGE,"E13.MirrorCS"),sQuery(id+"F0.wireOp",EDGE,"E14.MirrorCS"),sQuery(id+"F0.wireOp",EDGE,"E15.MirrorCS"),sQuery(id+"F0.wireOp",EDGE,"E16.MirrorCS"),sQuery(id+"F0.wireOp",EDGE,"E17.MirrorCS")])]});
            shell(context, id + "F24", {"isHollow" : true, "entities" : qUnion([Q0, Q1, Q2, Q3, Q4, Q5, Q6, Q7, Q8, Q9, Q10, Q11, Q12, Q13, Q14, Q15, Q16, Q17, Q18, Q19, Q20, Q21, Q22, Q23, Q24, Q25, Q26, Q27, Q28, Q29, Q30, Q31, Q32, Q33, Q34, Q35, Q36, Q37, Q38, Q39, Q40, Q41, Q42, Q43, Q44, Q45, Q46, Q47, Q48, Q49, Q50, Q51, Q52, Q53, Q54, Q55, Q56, Q57, Q58, Q59, Q60, Q61, Q62, Q63, Q64, Q65, Q66, Q67, Q68, Q69, Q70, Q71, Q72, Q73, Q74, Q75, Q76, Q77, Q78, Q79, Q80, Q81, Q82, Q83, Q84, Q85, Q86, Q87, Q88, Q89, Q90, Q91, Q92, Q93, Q94, Q95, Q96, Q97, Q98, Q99, Q100, Q101, Q102, Q103, Q104, Q105, Q106, Q107]), "parts" : qUnion([Q108]), "thickness" : 2.5 * mm});
        }
        {
            var Q0;
            Q0=makeQuery(id+"F1.opExtrude","CAP_FACE",FACE,{"disambiguationData":[OSD([sQuery(id+"F0.wireOp",EDGE,"E2"),sQuery(id+"F0.wireOp",EDGE,"E3"),sQuery(id+"F0.wireOp",EDGE,"E4"),sQuery(id+"F0.wireOp",EDGE,"E5"),sQuery(id+"F0.wireOp",EDGE,"E6"),sQuery(id+"F0.wireOp",EDGE,"E7"),sQuery(id+"F0.wireOp",EDGE,"E8"),sQuery(id+"F0.wireOp",EDGE,"E9"),sQuery(id+"F0.wireOp",EDGE,"E10.MirrorCS"),sQuery(id+"F0.wireOp",EDGE,"E11.MirrorCS"),sQuery(id+"F0.wireOp",EDGE,"E12.MirrorCS"),sQuery(id+"F0.wireOp",EDGE,"E13.MirrorCS"),sQuery(id+"F0.wireOp",EDGE,"E14.MirrorCS"),sQuery(id+"F0.wireOp",EDGE,"E15.MirrorCS"),sQuery(id+"F0.wireOp",EDGE,"E16.MirrorCS"),sQuery(id+"F0.wireOp",EDGE,"E17.MirrorCS")])],"isStart":true});
            var sketch = newSketch(context, id + "F25", { "sketchPlane" : qUnion([Q0])});
            skCircle(sketch, "E49", {"center": v(0, 30) * mm, "radius": 12.5 * mm});
            skCircle(sketch, "E50", {"center": v(0, 30) * mm, "radius": 9 * mm});
            skSolve(sketch);
        }
        {
            var Q0;
            Q0=makeQuery(id+"F25.imprint","IMPRINT",FACE,{"disambiguationData":[TD([[makeQuery(id+"F25.imprint","IMPRINT",EDGE,{"derivedFrom":sQuery(id+"F25.wireOp",EDGE,"E49")}),1.0]])]});
            extrude(context, id + "F26", {"entities" : qUnion([Q0]), "operationType" : NewBodyOperationType.REMOVE, "oppositeDirection" : true, "depth" : 2 * mm});
        }
        {
            var Q0;
            {var subQ0=sQuery(id+"F0.wireOp",EDGE,"E10.MirrorCS");var subQ1=sQuery(id+"F0.wireOp",EDGE,"E9");var subQ2=sQuery(id+"F0.wireOp",EDGE,"E8");var subQ3=sQuery(id+"F0.wireOp",EDGE,"E7");var subQ4=sQuery(id+"F0.wireOp",EDGE,"E6");var subQ6=sQuery(id+"F0.wireOp",EDGE,"E11.MirrorCS");var subQ7=sQuery(id+"F0.wireOp",EDGE,"E2");var subQ8=sQuery(id+"F0.wireOp",EDGE,"E5");var subQ9=sQuery(id+"F0.wireOp",EDGE,"E3");var subQ10=sQuery(id+"F0.wireOp",EDGE,"E17.MirrorCS");var subQ11=sQuery(id+"F0.wireOp",EDGE,"E4");var subQ12=sQuery(id+"F0.wireOp",EDGE,"E12.MirrorCS");var subQ13=sQuery(id+"F0.wireOp",EDGE,"E13.MirrorCS");var subQ14=sQuery(id+"F0.wireOp",EDGE,"E14.MirrorCS");var subQ15=sQuery(id+"F0.wireOp",EDGE,"E15.MirrorCS");var subQ16=sQuery(id+"F0.wireOp",EDGE,"E16.MirrorCS");Q0=makeQuery(id+"F26.boolean.opBoolean","SPLIT",FACE,{"disambiguationData":[TD([makeQuery(id+"F1.opExtrude","SWEPT_FACE",FACE,{"disambiguationData":[OSD([subQ7])]})])],"derivedFrom":makeQuery(id+"F1.opExtrude","CAP_FACE",FACE,{"disambiguationData":[OSD([subQ7,subQ9,subQ11,subQ8,subQ4,subQ3,subQ2,subQ1,subQ0,subQ6,subQ12,subQ13,subQ14,subQ15,subQ16,subQ10])],"isStart":true})});}
            var sketch = newSketch(context, id + "F27", { "sketchPlane" : qUnion([Q0])});
            skCircle(sketch, "E51", {"center": v(0, 30) * mm, "radius": 9 * mm});
            skSolve(sketch);
        }
        {
            var Q0;
            Q0=makeQuery(id+"F27.imprint","IMPRINT",FACE,{"disambiguationData":[TD([[makeQuery(id+"F27.imprint","IMPRINT",EDGE,{"derivedFrom":sQuery(id+"F27.wireOp",EDGE,"E51")}),1.0]])]});
            extrude(context, id + "F28", {"entities" : qUnion([Q0]), "operationType" : NewBodyOperationType.REMOVE, "oppositeDirection" : true, "depth" : 4 * mm});
        }
        {
            var Q0;
            {var subQ0=sQuery(id+"F0.wireOp",EDGE,"E10.MirrorCS");var subQ1=sQuery(id+"F0.wireOp",EDGE,"E9");var subQ2=sQuery(id+"F0.wireOp",EDGE,"E8");var subQ3=sQuery(id+"F0.wireOp",EDGE,"E7");var subQ4=sQuery(id+"F0.wireOp",EDGE,"E6");var subQ6=sQuery(id+"F0.wireOp",EDGE,"E11.MirrorCS");var subQ7=sQuery(id+"F0.wireOp",EDGE,"E2");var subQ8=sQuery(id+"F0.wireOp",EDGE,"E5");var subQ9=sQuery(id+"F0.wireOp",EDGE,"E3");var subQ10=sQuery(id+"F0.wireOp",EDGE,"E17.MirrorCS");var subQ11=sQuery(id+"F0.wireOp",EDGE,"E4");var subQ12=sQuery(id+"F0.wireOp",EDGE,"E12.MirrorCS");var subQ13=sQuery(id+"F0.wireOp",EDGE,"E13.MirrorCS");var subQ14=sQuery(id+"F0.wireOp",EDGE,"E14.MirrorCS");var subQ15=sQuery(id+"F0.wireOp",EDGE,"E15.MirrorCS");var subQ16=sQuery(id+"F0.wireOp",EDGE,"E16.MirrorCS");Q0=makeQuery(id+"F26.boolean.opBoolean","SPLIT",FACE,{"disambiguationData":[TD([makeQuery(id+"F1.opExtrude","SWEPT_FACE",FACE,{"disambiguationData":[OSD([subQ7])]})])],"derivedFrom":makeQuery(id+"F1.opExtrude","CAP_FACE",FACE,{"disambiguationData":[OSD([subQ7,subQ9,subQ11,subQ8,subQ4,subQ3,subQ2,subQ1,subQ0,subQ6,subQ12,subQ13,subQ14,subQ15,subQ16,subQ10])],"isStart":true})});}
            var sketch = newSketch(context, id + "F29", { "sketchPlane" : qUnion([Q0])});
            skCircle(sketch, "E52", {"center": v(-40.53, 14.36) * mm, "radius": 4.25 * mm});
            skCircle(sketch, "E53", {"center": v(39.86, 14.53) * mm, "radius": 4.25 * mm});
            skSolve(sketch);
        }
        {
            var Q0;
            Q0=makeQuery(id+"F29.imprint","IMPRINT",FACE,{"disambiguationData":[TD([[makeQuery(id+"F29.imprint","IMPRINT",EDGE,{"derivedFrom":sQuery(id+"F29.wireOp",EDGE,"E52")}),1.0]])]});
            var Q1;
            Q1=makeQuery(id+"F29.imprint","IMPRINT",FACE,{"disambiguationData":[TD([[makeQuery(id+"F29.imprint","IMPRINT",EDGE,{"derivedFrom":sQuery(id+"F29.wireOp",EDGE,"E53")}),1.0]])]});
            extrude(context, id + "F30", {"entities" : qUnion([Q0, Q1]), "operationType" : NewBodyOperationType.REMOVE, "oppositeDirection" : true, "depth" : 10 * mm});
        }
        {
            var Q0;
            Q0=makeQuery(id+"F1.opExtrude","CAP_FACE",FACE,{"disambiguationData":[OSD([sQuery(id+"F0.wireOp",EDGE,"E2"),sQuery(id+"F0.wireOp",EDGE,"E3"),sQuery(id+"F0.wireOp",EDGE,"E4"),sQuery(id+"F0.wireOp",EDGE,"E5"),sQuery(id+"F0.wireOp",EDGE,"E6"),sQuery(id+"F0.wireOp",EDGE,"E7"),sQuery(id+"F0.wireOp",EDGE,"E8"),sQuery(id+"F0.wireOp",EDGE,"E9"),sQuery(id+"F0.wireOp",EDGE,"E10.MirrorCS"),sQuery(id+"F0.wireOp",EDGE,"E11.MirrorCS"),sQuery(id+"F0.wireOp",EDGE,"E12.MirrorCS"),sQuery(id+"F0.wireOp",EDGE,"E13.MirrorCS"),sQuery(id+"F0.wireOp",EDGE,"E14.MirrorCS"),sQuery(id+"F0.wireOp",EDGE,"E15.MirrorCS"),sQuery(id+"F0.wireOp",EDGE,"E16.MirrorCS"),sQuery(id+"F0.wireOp",EDGE,"E17.MirrorCS")])],"isStart":false});
            var sketch = newSketch(context, id + "F31", { "sketchPlane" : qUnion([Q0])});
            skArc(sketch, "E54", {"start": v(55.5, -20) * mm, "mid": v(52.03, 27.83) * mm, "end": v(14.18, 57.27) * mm});
            skLineSegment(sketch, "E55", {"start": v(55.5, -20) * mm, "end": v(-45, -20) * mm});
            skLineSegment(sketch, "E56", {"start": v(-18.64, 65) * mm, "end": v(-11.64, 52.88) * mm});
            skLineSegment(sketch, "E57", {"start": v(18.64, 65) * mm, "end": v(11.64, 52.88) * mm});
            skArc(sketch, "E58.trimOffspring", {"start": v(-14.18, 57.27) * mm, "mid": v(-40.28, 43.1) * mm, "end": v(-56.18, 18.02) * mm});
            skLineSegment(sketch, "E59", {"start": v(-45, -20) * mm, "end": v(-45, -15) * mm});
            skLineSegment(sketch, "E60", {"start": v(-45, -15) * mm, "end": v(-40, -15) * mm});
            skLineSegment(sketch, "E61", {"start": v(-40, -15) * mm, "end": v(-40, -10) * mm});
            skLineSegment(sketch, "E62", {"start": v(-40, -10) * mm, "end": v(-67.14, 37) * mm});
            skSolve(sketch);
        }
        {
            var Q0;
            Q0 = qSketchRegion(id + "F31", true);
            var Q1;
            {var subQ2=sQuery(id+"F31.wireOp",EDGE,"E58.trimOffspring");Q1=makeQuery(id+"F31.imprint","IMPRINT",FACE,{"disambiguationData":[TD([[makeQuery(id+"F31.imprint","IMPRINT",EDGE,{"derivedFrom":subQ2}),1.0]])]});}
            var Q2;
            {var subQ4=makeQuery(id+"F1.opExtrude","CAP_EDGE",EDGE,{"disambiguationData":[OSD([sQuery(id+"F0.wireOp",EDGE,"E14.MirrorCS")])],"isStart":false});Q2=makeQuery(id+"F31.imprint","IMPRINT",FACE,{"disambiguationData":[TD([[makeQuery(id+"F31.imprint","IMPRINT",EDGE,{"derivedFrom":subQ4}),-1.0]])]});}
            extrude(context, id + "F32", {"entities" : qUnion([Q0, Q1, Q2]), "operationType" : NewBodyOperationType.ADD, "depth" : 5 * mm});
        }
        {
            var Q0;
            Q0=makeQuery(id+"F32.opExtrude","CAP_FACE",FACE,{"disambiguationData":[OSD([sQuery(id+"F0.wireOp",EDGE,"E9"),sQuery(id+"F0.wireOp",EDGE,"E10.MirrorCS"),sQuery(id+"F8.wireOp",EDGE,"E23"),sQuery(id+"F10.wireOp",EDGE,"E24.bottom"),sQuery(id+"F10.wireOp",EDGE,"E24.left"),sQuery(id+"F10.wireOp",EDGE,"E24.right"),sQuery(id+"F31.wireOp",EDGE,"E54"),sQuery(id+"F31.wireOp",EDGE,"E55"),sQuery(id+"F31.wireOp",EDGE,"E56"),sQuery(id+"F31.wireOp",EDGE,"E57"),sQuery(id+"F31.wireOp",EDGE,"E58.trimOffspring"),sQuery(id+"F31.wireOp",EDGE,"E59"),sQuery(id+"F31.wireOp",EDGE,"E60"),sQuery(id+"F31.wireOp",EDGE,"E61"),sQuery(id+"F31.wireOp",EDGE,"E62")])],"isStart":false});
            var sketch = newSketch(context, id + "F33", { "sketchPlane" : qUnion([Q0])});
            skCircle(sketch, "E63", {"center": v(0, 0) * mm, "radius": 10 * mm});
            skSolve(sketch);
        }
        {
            var Q0;
            Q0 = qSketchRegion(id + "F33", true);
            extrude(context, id + "F34", {"entities" : qUnion([Q0]), "operationType" : NewBodyOperationType.REMOVE, "oppositeDirection" : true, "depth" : 10 * mm});
        }
        {
            var Q0;
            Q0=makeQuery(id+"F32.opExtrude","CAP_FACE",FACE,{"disambiguationData":[OSD([sQuery(id+"F0.wireOp",EDGE,"E9"),sQuery(id+"F0.wireOp",EDGE,"E10.MirrorCS"),sQuery(id+"F8.wireOp",EDGE,"E23"),sQuery(id+"F10.wireOp",EDGE,"E24.bottom"),sQuery(id+"F10.wireOp",EDGE,"E24.left"),sQuery(id+"F10.wireOp",EDGE,"E24.right"),sQuery(id+"F31.wireOp",EDGE,"E54"),sQuery(id+"F31.wireOp",EDGE,"E55"),sQuery(id+"F31.wireOp",EDGE,"E56"),sQuery(id+"F31.wireOp",EDGE,"E57"),sQuery(id+"F31.wireOp",EDGE,"E58.trimOffspring"),sQuery(id+"F31.wireOp",EDGE,"E59"),sQuery(id+"F31.wireOp",EDGE,"E60"),sQuery(id+"F31.wireOp",EDGE,"E61"),sQuery(id+"F31.wireOp",EDGE,"E62")])],"isStart":false});
            var sketch = newSketch(context, id + "F35", { "sketchPlane" : qUnion([Q0])});
            skCircle(sketch, "E64", {"center": v(0, 0) * mm, "radius": 47.5 * mm});
            skSolve(sketch);
        }
        {
            var Q0;
            Q0 = qSketchRegion(id + "F35", true);
            extrude(context, id + "F36", {"entities" : qUnion([Q0]), "operationType" : NewBodyOperationType.REMOVE, "oppositeDirection" : true, "depth" : 5 * mm});
        }
    });
